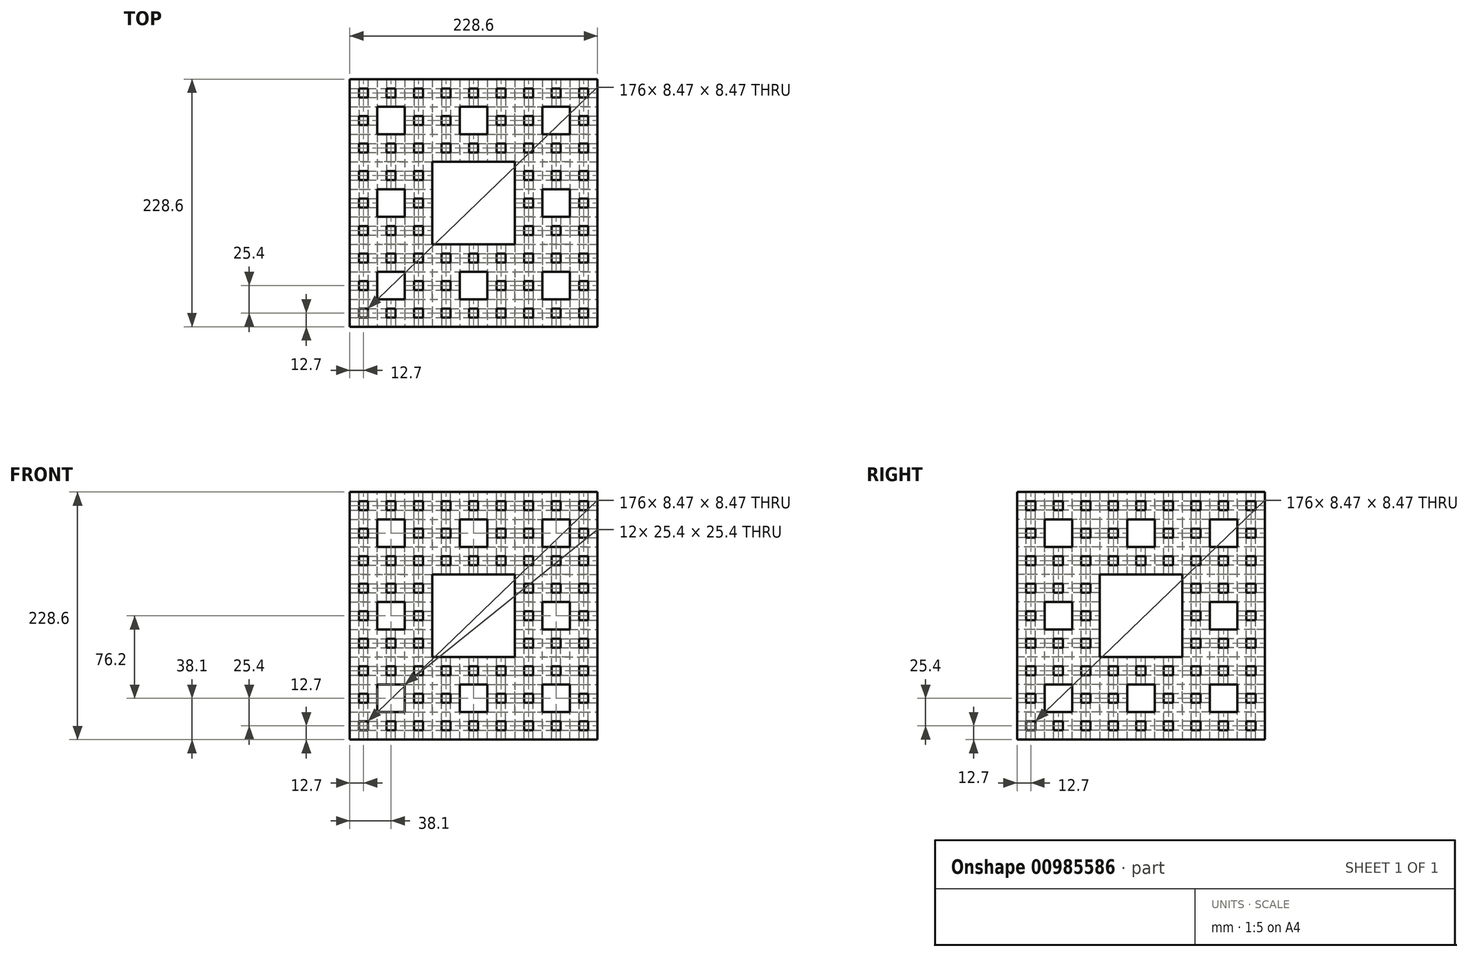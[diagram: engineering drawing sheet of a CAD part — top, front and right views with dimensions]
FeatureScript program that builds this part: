
annotation { "Feature Type Name" : "Feature", "Feature Type Description" : "" }
export const myFeature = defineFeature(function(context is Context, id is Id, definition is map)
    precondition{}
    {
        {
            var Q0;
            Q0=qCreatedBy(makeId("Front.planeOp"),FACE);
            var sketch = newSketch(context, id + "F0", { "sketchPlane" : qUnion([Q0])});
            skLineSegment(sketch, "E0.bottom", {"start": v(114.3, 114.3) * mm, "end": v(-114.3, 114.3) * mm});
            skLineSegment(sketch, "E0.top", {"start": v(114.3, -114.3) * mm, "end": v(-114.3, -114.3) * mm});
            skLineSegment(sketch, "E0.left", {"start": v(114.3, 114.3) * mm, "end": v(114.3, -114.3) * mm});
            skLineSegment(sketch, "E0.right", {"start": v(-114.3, 114.3) * mm, "end": v(-114.3, -114.3) * mm});
            skPoint(sketch, "E0.middle", {"position": v(0, 0) * mm});
            skSolve(sketch);
        }
        {
            var Q0;
            Q0 = qSketchRegion(id + "F0", true);
            extrude(context, id + "F1", {"entities" : qUnion([Q0]), "endBound" : BoundingType.SYMMETRIC, "depth" : 228.6 * mm, "offsetDistance" : 25.4 * mm});
        }
        {
            var Q0;
            Q0=qCreatedBy(makeId("Front.planeOp"),FACE);
            var Q1;
            Q1=qCreatedBy(makeId("Front.planeOp"),FACE);
            var sketch = newSketch(context, id + "F2", { "sketchPlane" : qUnion([Q0, Q1])});
            skLineSegment(sketch, "E1.bottom", {"start": v(38.1, 38.1) * mm, "end": v(-38.1, 38.1) * mm});
            skLineSegment(sketch, "E1.top", {"start": v(38.1, -38.1) * mm, "end": v(-38.1, -38.1) * mm});
            skLineSegment(sketch, "E1.left", {"start": v(38.1, 38.1) * mm, "end": v(38.1, -38.1) * mm});
            skLineSegment(sketch, "E1.right", {"start": v(-38.1, 38.1) * mm, "end": v(-38.1, -38.1) * mm});
            skPoint(sketch, "E1.middle", {"position": v(0, 0) * mm});
            skSolve(sketch);
        }
        {
            var Q0;
            Q0 = qSketchRegion(id + "F2", true);
            extrude(context, id + "F3", {"entities" : qUnion([Q0]), "operationType" : NewBodyOperationType.REMOVE, "endBound" : BoundingType.SYMMETRIC, "oppositeDirection" : true, "depth" : 228.6 * mm, "offsetDistance" : 25.4 * mm});
        }
        {
            var Q0;
            Q0=qCreatedBy(makeId("Right.planeOp"),FACE);
            var Q1;
            Q1=qCreatedBy(makeId("Right.planeOp"),FACE);
            var sketch = newSketch(context, id + "F4", { "sketchPlane" : qUnion([Q0, Q1])});
            skLineSegment(sketch, "E2.bottom", {"start": v(38.1, 38.1) * mm, "end": v(-38.1, 38.1) * mm});
            skLineSegment(sketch, "E2.top", {"start": v(38.1, -38.1) * mm, "end": v(-38.1, -38.1) * mm});
            skLineSegment(sketch, "E2.left", {"start": v(38.1, 38.1) * mm, "end": v(38.1, -38.1) * mm});
            skLineSegment(sketch, "E2.right", {"start": v(-38.1, 38.1) * mm, "end": v(-38.1, -38.1) * mm});
            skPoint(sketch, "E2.middle", {"position": v(0, 0) * mm});
            skSolve(sketch);
        }
        {
            var Q0;
            Q0 = qSketchRegion(id + "F4", true);
            extrude(context, id + "F5", {"entities" : qUnion([Q0]), "operationType" : NewBodyOperationType.REMOVE, "endBound" : BoundingType.SYMMETRIC, "oppositeDirection" : true, "depth" : 228.6 * mm, "offsetDistance" : 25.4 * mm});
        }
        {
            var Q0;
            Q0=qCreatedBy(makeId("Top.planeOp"),FACE);
            var Q1;
            Q1=qCreatedBy(makeId("Top.planeOp"),FACE);
            var sketch = newSketch(context, id + "F6", { "sketchPlane" : qUnion([Q0, Q1])});
            skLineSegment(sketch, "E3.bottom", {"start": v(-38.1, -38.1) * mm, "end": v(38.1, -38.1) * mm});
            skLineSegment(sketch, "E3.top", {"start": v(-38.1, 38.1) * mm, "end": v(38.1, 38.1) * mm});
            skLineSegment(sketch, "E3.left", {"start": v(-38.1, -38.1) * mm, "end": v(-38.1, 38.1) * mm});
            skLineSegment(sketch, "E3.right", {"start": v(38.1, -38.1) * mm, "end": v(38.1, 38.1) * mm});
            skPoint(sketch, "E3.middle", {"position": v(0, 0) * mm});
            skSolve(sketch);
        }
        {
            var Q0;
            Q0 = qSketchRegion(id + "F6", true);
            extrude(context, id + "F7", {"entities" : qUnion([Q0]), "operationType" : NewBodyOperationType.REMOVE, "endBound" : BoundingType.SYMMETRIC, "depth" : 228.6 * mm, "offsetDistance" : 25.4 * mm});
        }
        {
            var Q0;
            Q0=makeQuery(id+"F1.opExtrude","SWEPT_FACE",FACE,{"disambiguationData":[OSD([sQuery(id+"F0.wireOp",EDGE,"E0.left")])]});
            var sketch = newSketch(context, id + "F8", { "sketchPlane" : qUnion([Q0])});
            skSolve(sketch);
        }
        {
            var Q0;
            Q0=makeQuery(id+"F1.opExtrude","CAP_FACE",FACE,{"disambiguationData":[OSD([sQuery(id+"F0.wireOp",EDGE,"E0.bottom"),sQuery(id+"F0.wireOp",EDGE,"E0.top"),sQuery(id+"F0.wireOp",EDGE,"E0.left"),sQuery(id+"F0.wireOp",EDGE,"E0.right")])],"isStart":false});
            var sketch = newSketch(context, id + "F9", { "sketchPlane" : qUnion([Q0])});
            skPoint(sketch, "E4", {"position": v(76.2, 76.2) * mm});
            skPoint(sketch, "E5", {"position": v(0, 76.2) * mm});
            skPoint(sketch, "E6", {"position": v(-76.2, 76.2) * mm});
            skPoint(sketch, "E7", {"position": v(-76.2, 0) * mm});
            skPoint(sketch, "E8", {"position": v(76.2, 0) * mm});
            skPoint(sketch, "E9", {"position": v(76.2, -76.2) * mm});
            skPoint(sketch, "E10", {"position": v(0, -76.2) * mm});
            skPoint(sketch, "E11", {"position": v(-76.2, -76.2) * mm});
            skLineSegment(sketch, "E12.bottom", {"start": v(-63.5, 63.5) * mm, "end": v(-88.9, 63.5) * mm});
            skLineSegment(sketch, "E12.top", {"start": v(-63.5, 88.9) * mm, "end": v(-88.9, 88.9) * mm});
            skLineSegment(sketch, "E12.left", {"start": v(-63.5, 63.5) * mm, "end": v(-63.5, 88.9) * mm});
            skLineSegment(sketch, "E12.right", {"start": v(-88.9, 63.5) * mm, "end": v(-88.9, 88.9) * mm});
            skLineSegment(sketch, "E13.bottom", {"start": v(88.9, 63.5) * mm, "end": v(63.5, 63.5) * mm});
            skLineSegment(sketch, "E13.top", {"start": v(88.9, 88.9) * mm, "end": v(63.5, 88.9) * mm});
            skLineSegment(sketch, "E13.left", {"start": v(88.9, 63.5) * mm, "end": v(88.9, 88.9) * mm});
            skLineSegment(sketch, "E13.right", {"start": v(63.5, 63.5) * mm, "end": v(63.5, 88.9) * mm});
            skLineSegment(sketch, "E14.bottom", {"start": v(12.7, 63.5) * mm, "end": v(-12.7, 63.5) * mm});
            skLineSegment(sketch, "E14.top", {"start": v(12.7, 88.9) * mm, "end": v(-12.7, 88.9) * mm});
            skLineSegment(sketch, "E14.left", {"start": v(12.7, 63.5) * mm, "end": v(12.7, 88.9) * mm});
            skLineSegment(sketch, "E14.right", {"start": v(-12.7, 63.5) * mm, "end": v(-12.7, 88.9) * mm});
            skLineSegment(sketch, "E15.bottom", {"start": v(88.9, -12.7) * mm, "end": v(63.5, -12.7) * mm});
            skLineSegment(sketch, "E15.top", {"start": v(88.9, 12.7) * mm, "end": v(63.5, 12.7) * mm});
            skLineSegment(sketch, "E15.left", {"start": v(88.9, -12.7) * mm, "end": v(88.9, 12.7) * mm});
            skLineSegment(sketch, "E15.right", {"start": v(63.5, -12.7) * mm, "end": v(63.5, 12.7) * mm});
            skLineSegment(sketch, "E16.bottom", {"start": v(63.5, -63.5) * mm, "end": v(88.9, -63.5) * mm});
            skLineSegment(sketch, "E16.top", {"start": v(63.5, -88.9) * mm, "end": v(88.9, -88.9) * mm});
            skLineSegment(sketch, "E16.left", {"start": v(63.5, -63.5) * mm, "end": v(63.5, -88.9) * mm});
            skLineSegment(sketch, "E16.right", {"start": v(88.9, -63.5) * mm, "end": v(88.9, -88.9) * mm});
            skLineSegment(sketch, "E17.bottom", {"start": v(12.7, -63.5) * mm, "end": v(-12.7, -63.5) * mm});
            skLineSegment(sketch, "E17.top", {"start": v(12.7, -88.9) * mm, "end": v(-12.7, -88.9) * mm});
            skLineSegment(sketch, "E17.left", {"start": v(12.7, -63.5) * mm, "end": v(12.7, -88.9) * mm});
            skLineSegment(sketch, "E17.right", {"start": v(-12.7, -63.5) * mm, "end": v(-12.7, -88.9) * mm});
            skLineSegment(sketch, "E18.bottom", {"start": v(-63.5, -63.5) * mm, "end": v(-88.9, -63.5) * mm});
            skLineSegment(sketch, "E18.top", {"start": v(-63.5, -88.9) * mm, "end": v(-88.9, -88.9) * mm});
            skLineSegment(sketch, "E18.left", {"start": v(-63.5, -63.5) * mm, "end": v(-63.5, -88.9) * mm});
            skLineSegment(sketch, "E18.right", {"start": v(-88.9, -63.5) * mm, "end": v(-88.9, -88.9) * mm});
            skLineSegment(sketch, "E19.bottom", {"start": v(-63.5, 12.7) * mm, "end": v(-88.9, 12.7) * mm});
            skLineSegment(sketch, "E19.top", {"start": v(-63.5, -12.7) * mm, "end": v(-88.9, -12.7) * mm});
            skLineSegment(sketch, "E19.left", {"start": v(-63.5, 12.7) * mm, "end": v(-63.5, -12.7) * mm});
            skLineSegment(sketch, "E19.right", {"start": v(-88.9, 12.7) * mm, "end": v(-88.9, -12.7) * mm});
            skSolve(sketch);
        }
        {
            var Q0;
            Q0 = qSketchRegion(id + "F9", true);
            extrude(context, id + "F10", {"entities" : qUnion([Q0]), "operationType" : NewBodyOperationType.REMOVE, "oppositeDirection" : true, "depth" : 228.6 * mm, "offsetDistance" : 25.4 * mm});
        }
        {
            var Q0;
            Q0=makeQuery(id+"F1.opExtrude","CAP_FACE",FACE,{"disambiguationData":[OSD([sQuery(id+"F0.wireOp",EDGE,"E0.bottom"),sQuery(id+"F0.wireOp",EDGE,"E0.top"),sQuery(id+"F0.wireOp",EDGE,"E0.left"),sQuery(id+"F0.wireOp",EDGE,"E0.right")])],"isStart":false});
            var sketch = newSketch(context, id + "F11", { "sketchPlane" : qUnion([Q0])});
            skPoint(sketch, "E20", {"position": v(-101.6, 101.6) * mm});
            skPoint(sketch, "E21", {"position": v(-76.2, 101.6) * mm});
            skPoint(sketch, "E22", {"position": v(-50.8, 101.6) * mm});
            skPoint(sketch, "E23", {"position": v(-50.8, 76.2) * mm});
            skPoint(sketch, "E24", {"position": v(-50.8, 50.8) * mm});
            skPoint(sketch, "E25", {"position": v(-76.2, 50.8) * mm});
            skPoint(sketch, "E26", {"position": v(-101.6, 50.8) * mm});
            skPoint(sketch, "E27", {"position": v(-101.6, 76.2) * mm});
            skPoint(sketch, "E28", {"position": v(-76.2, 88.9) * mm});
            skPoint(sketch, "E29", {"position": v(-76.2, 63.5) * mm});
            skPoint(sketch, "E30", {"position": v(-88.9, 76.2) * mm});
            skPoint(sketch, "E31", {"position": v(-63.5, 76.2) * mm});
            skLineSegment(sketch, "E32.bottom", {"start": v(-97.37, 105.83) * mm, "end": v(-105.83, 105.83) * mm});
            skLineSegment(sketch, "E32.top", {"start": v(-97.37, 97.37) * mm, "end": v(-105.83, 97.37) * mm});
            skLineSegment(sketch, "E32.left", {"start": v(-97.37, 105.83) * mm, "end": v(-97.37, 97.37) * mm});
            skLineSegment(sketch, "E32.right", {"start": v(-105.83, 105.83) * mm, "end": v(-105.83, 97.37) * mm});
            skLineSegment(sketch, "E33.bottom", {"start": v(-71.97, 105.83) * mm, "end": v(-80.43, 105.83) * mm});
            skLineSegment(sketch, "E33.top", {"start": v(-71.97, 97.37) * mm, "end": v(-80.43, 97.37) * mm});
            skLineSegment(sketch, "E33.left", {"start": v(-71.97, 105.83) * mm, "end": v(-71.97, 97.37) * mm});
            skLineSegment(sketch, "E33.right", {"start": v(-80.43, 105.83) * mm, "end": v(-80.43, 97.37) * mm});
            skLineSegment(sketch, "E34.bottom", {"start": v(-46.57, 105.83) * mm, "end": v(-55.03, 105.83) * mm});
            skLineSegment(sketch, "E34.top", {"start": v(-46.57, 97.37) * mm, "end": v(-55.03, 97.37) * mm});
            skLineSegment(sketch, "E34.left", {"start": v(-46.57, 105.83) * mm, "end": v(-46.57, 97.37) * mm});
            skLineSegment(sketch, "E34.right", {"start": v(-55.03, 105.83) * mm, "end": v(-55.03, 97.37) * mm});
            skLineSegment(sketch, "E35.bottom", {"start": v(-46.57, 80.43) * mm, "end": v(-55.03, 80.43) * mm});
            skLineSegment(sketch, "E35.top", {"start": v(-46.57, 71.97) * mm, "end": v(-55.03, 71.97) * mm});
            skLineSegment(sketch, "E35.left", {"start": v(-46.57, 80.43) * mm, "end": v(-46.57, 71.97) * mm});
            skLineSegment(sketch, "E35.right", {"start": v(-55.03, 80.43) * mm, "end": v(-55.03, 71.97) * mm});
            skLineSegment(sketch, "E36.bottom", {"start": v(-55.03, 55.03) * mm, "end": v(-46.57, 55.03) * mm});
            skLineSegment(sketch, "E36.top", {"start": v(-55.03, 46.57) * mm, "end": v(-46.57, 46.57) * mm});
            skLineSegment(sketch, "E36.left", {"start": v(-55.03, 55.03) * mm, "end": v(-55.03, 46.57) * mm});
            skLineSegment(sketch, "E36.right", {"start": v(-46.57, 55.03) * mm, "end": v(-46.57, 46.57) * mm});
            skLineSegment(sketch, "E37.bottom", {"start": v(-71.97, 55.03) * mm, "end": v(-80.43, 55.03) * mm});
            skLineSegment(sketch, "E37.top", {"start": v(-71.97, 46.57) * mm, "end": v(-80.43, 46.57) * mm});
            skLineSegment(sketch, "E37.left", {"start": v(-71.97, 55.03) * mm, "end": v(-71.97, 46.57) * mm});
            skLineSegment(sketch, "E37.right", {"start": v(-80.43, 55.03) * mm, "end": v(-80.43, 46.57) * mm});
            skLineSegment(sketch, "E38.bottom", {"start": v(-97.37, 55.03) * mm, "end": v(-105.83, 55.03) * mm});
            skLineSegment(sketch, "E38.top", {"start": v(-97.37, 46.57) * mm, "end": v(-105.83, 46.57) * mm});
            skLineSegment(sketch, "E38.left", {"start": v(-97.37, 55.03) * mm, "end": v(-97.37, 46.57) * mm});
            skLineSegment(sketch, "E38.right", {"start": v(-105.83, 55.03) * mm, "end": v(-105.83, 46.57) * mm});
            skLineSegment(sketch, "E39.bottom", {"start": v(-97.37, 80.43) * mm, "end": v(-105.83, 80.43) * mm});
            skLineSegment(sketch, "E39.top", {"start": v(-97.37, 71.97) * mm, "end": v(-105.83, 71.97) * mm});
            skLineSegment(sketch, "E39.left", {"start": v(-97.37, 80.43) * mm, "end": v(-97.37, 71.97) * mm});
            skLineSegment(sketch, "E39.right", {"start": v(-105.83, 80.43) * mm, "end": v(-105.83, 71.97) * mm});
            skLineSegment(sketch, "E40.MirrorCS", {"start": v(71.97, 55.03) * mm, "end": v(80.43, 55.03) * mm});
            skLineSegment(sketch, "E41.MirrorCS", {"start": v(55.03, 80.43) * mm, "end": v(55.03, 71.97) * mm});
            skLineSegment(sketch, "E42.MirrorCS", {"start": v(46.57, 80.43) * mm, "end": v(46.57, 71.97) * mm});
            skLineSegment(sketch, "E43.MirrorCS", {"start": v(97.37, 80.43) * mm, "end": v(97.37, 71.97) * mm});
            skLineSegment(sketch, "E44.MirrorCS", {"start": v(71.97, 55.03) * mm, "end": v(71.97, 46.57) * mm});
            skLineSegment(sketch, "E45.MirrorCS", {"start": v(80.43, 105.83) * mm, "end": v(80.43, 97.37) * mm});
            skLineSegment(sketch, "E46.MirrorCS", {"start": v(46.57, 97.37) * mm, "end": v(55.03, 97.37) * mm});
            skLineSegment(sketch, "E47.MirrorCS", {"start": v(97.37, 105.83) * mm, "end": v(97.37, 97.37) * mm});
            skLineSegment(sketch, "E48.MirrorCS", {"start": v(71.97, 105.83) * mm, "end": v(71.97, 97.37) * mm});
            skLineSegment(sketch, "E49.MirrorCS", {"start": v(97.37, 71.97) * mm, "end": v(105.83, 71.97) * mm});
            skLineSegment(sketch, "E50.MirrorCS", {"start": v(71.97, 46.57) * mm, "end": v(80.43, 46.57) * mm});
            skLineSegment(sketch, "E51.MirrorCS", {"start": v(97.37, 80.43) * mm, "end": v(105.83, 80.43) * mm});
            skLineSegment(sketch, "E52.MirrorCS", {"start": v(55.03, 105.83) * mm, "end": v(55.03, 97.37) * mm});
            skLineSegment(sketch, "E53.MirrorCS", {"start": v(46.57, 105.83) * mm, "end": v(55.03, 105.83) * mm});
            skLineSegment(sketch, "E54.MirrorCS", {"start": v(80.43, 55.03) * mm, "end": v(80.43, 46.57) * mm});
            skLineSegment(sketch, "E55.MirrorCS", {"start": v(105.83, 55.03) * mm, "end": v(105.83, 46.57) * mm});
            skLineSegment(sketch, "E56.MirrorCS", {"start": v(97.37, 97.37) * mm, "end": v(105.83, 97.37) * mm});
            skLineSegment(sketch, "E57.MirrorCS", {"start": v(97.37, 105.83) * mm, "end": v(105.83, 105.83) * mm});
            skLineSegment(sketch, "E58.MirrorCS", {"start": v(97.37, 55.03) * mm, "end": v(97.37, 46.57) * mm});
            skLineSegment(sketch, "E59.MirrorCS", {"start": v(46.57, 80.43) * mm, "end": v(55.03, 80.43) * mm});
            skLineSegment(sketch, "E60.MirrorCS", {"start": v(105.83, 105.83) * mm, "end": v(105.83, 97.37) * mm});
            skLineSegment(sketch, "E61.MirrorCS", {"start": v(55.03, 46.57) * mm, "end": v(46.57, 46.57) * mm});
            skLineSegment(sketch, "E62.MirrorCS", {"start": v(55.03, 55.03) * mm, "end": v(55.03, 46.57) * mm});
            skLineSegment(sketch, "E63.MirrorCS", {"start": v(71.97, 105.83) * mm, "end": v(80.43, 105.83) * mm});
            skLineSegment(sketch, "E64.MirrorCS", {"start": v(71.97, 97.37) * mm, "end": v(80.43, 97.37) * mm});
            skLineSegment(sketch, "E65.MirrorCS", {"start": v(97.37, 55.03) * mm, "end": v(105.83, 55.03) * mm});
            skLineSegment(sketch, "E66.MirrorCS", {"start": v(105.83, 80.43) * mm, "end": v(105.83, 71.97) * mm});
            skLineSegment(sketch, "E67.MirrorCS", {"start": v(97.37, 46.57) * mm, "end": v(105.83, 46.57) * mm});
            skLineSegment(sketch, "E68.MirrorCS", {"start": v(55.03, 55.03) * mm, "end": v(46.57, 55.03) * mm});
            skLineSegment(sketch, "E69.MirrorCS", {"start": v(46.57, 71.97) * mm, "end": v(55.03, 71.97) * mm});
            skLineSegment(sketch, "E70.MirrorCS", {"start": v(46.57, 105.83) * mm, "end": v(46.57, 97.37) * mm});
            skLineSegment(sketch, "E71.MirrorCS", {"start": v(46.57, 55.03) * mm, "end": v(46.57, 46.57) * mm});
            skPoint(sketch, "E72.MirrorP", {"position": v(50.8, 101.6) * mm});
            skPoint(sketch, "E73.MirrorP", {"position": v(101.6, 76.2) * mm});
            skPoint(sketch, "E74.MirrorP", {"position": v(88.9, 76.2) * mm});
            skPoint(sketch, "E75.MirrorP", {"position": v(50.45, 76.2) * mm});
            skPoint(sketch, "E76.MirrorP", {"position": v(76.2, 101.6) * mm});
            skPoint(sketch, "E77.MirrorP", {"position": v(101.6, 50.8) * mm});
            skPoint(sketch, "E78.MirrorP", {"position": v(76.2, 50.8) * mm});
            skPoint(sketch, "E79.MirrorP", {"position": v(101.6, 101.6) * mm});
            skPoint(sketch, "E80.MirrorP", {"position": v(50.8, 50.8) * mm});
            skPoint(sketch, "E81.MirrorP", {"position": v(63.5, 76.2) * mm});
            skPoint(sketch, "E82.MirrorP", {"position": v(76.2, 88.9) * mm});
            skPoint(sketch, "E83.MirrorP", {"position": v(76.2, 63.5) * mm});
            skLineSegment(sketch, "E84.MirrorCS", {"start": v(-46.57, -80.43) * mm, "end": v(-55.03, -80.43) * mm});
            skLineSegment(sketch, "E85.MirrorCS", {"start": v(-46.57, -97.37) * mm, "end": v(-55.03, -97.37) * mm});
            skLineSegment(sketch, "E86.MirrorCS", {"start": v(-55.03, -105.83) * mm, "end": v(-55.03, -97.37) * mm});
            skLineSegment(sketch, "E87.MirrorCS", {"start": v(-46.57, -105.83) * mm, "end": v(-46.57, -97.37) * mm});
            skLineSegment(sketch, "E88.MirrorCS", {"start": v(-46.57, -105.83) * mm, "end": v(-55.03, -105.83) * mm});
            skLineSegment(sketch, "E89.MirrorCS", {"start": v(-71.97, -55.03) * mm, "end": v(-80.43, -55.03) * mm});
            skLineSegment(sketch, "E90.MirrorCS", {"start": v(-55.03, -80.43) * mm, "end": v(-55.03, -71.97) * mm});
            skLineSegment(sketch, "E91.MirrorCS", {"start": v(-105.83, -80.43) * mm, "end": v(-105.83, -71.97) * mm});
            skLineSegment(sketch, "E92.MirrorCS", {"start": v(-71.97, -46.57) * mm, "end": v(-80.43, -46.57) * mm});
            skLineSegment(sketch, "E93.MirrorCS", {"start": v(105.83, -105.83) * mm, "end": v(105.83, -97.37) * mm});
            skLineSegment(sketch, "E94.MirrorCS", {"start": v(97.37, -55.03) * mm, "end": v(97.37, -46.57) * mm});
            skPoint(sketch, "E95.MirrorP", {"position": v(-50.8, -101.6) * mm});
            skLineSegment(sketch, "E96.MirrorCS", {"start": v(46.57, -105.83) * mm, "end": v(46.57, -97.37) * mm});
            skLineSegment(sketch, "E97.MirrorCS", {"start": v(71.97, -46.57) * mm, "end": v(80.43, -46.57) * mm});
            skLineSegment(sketch, "E98.MirrorCS", {"start": v(-97.37, -105.83) * mm, "end": v(-97.37, -97.37) * mm});
            skLineSegment(sketch, "E99.MirrorCS", {"start": v(80.43, -55.03) * mm, "end": v(80.43, -46.57) * mm});
            skLineSegment(sketch, "E100.MirrorCS", {"start": v(-97.37, -55.03) * mm, "end": v(-97.37, -46.57) * mm});
            skLineSegment(sketch, "E101.MirrorCS", {"start": v(97.37, -105.83) * mm, "end": v(97.37, -97.37) * mm});
            skLineSegment(sketch, "E102.MirrorCS", {"start": v(-71.97, -105.83) * mm, "end": v(-71.97, -97.37) * mm});
            skLineSegment(sketch, "E103.MirrorCS", {"start": v(46.57, -105.83) * mm, "end": v(55.03, -105.83) * mm});
            skLineSegment(sketch, "E104.MirrorCS", {"start": v(-46.57, -71.97) * mm, "end": v(-55.03, -71.97) * mm});
            skLineSegment(sketch, "E105.MirrorCS", {"start": v(55.03, -55.03) * mm, "end": v(46.57, -55.03) * mm});
            skLineSegment(sketch, "E106.MirrorCS", {"start": v(55.03, -46.57) * mm, "end": v(46.57, -46.57) * mm});
            skLineSegment(sketch, "E107.MirrorCS", {"start": v(97.37, -55.03) * mm, "end": v(105.83, -55.03) * mm});
            skLineSegment(sketch, "E108.MirrorCS", {"start": v(-97.37, -80.43) * mm, "end": v(-105.83, -80.43) * mm});
            skLineSegment(sketch, "E109.MirrorCS", {"start": v(46.57, -80.43) * mm, "end": v(55.03, -80.43) * mm});
            skLineSegment(sketch, "E110.MirrorCS", {"start": v(97.37, -80.43) * mm, "end": v(105.83, -80.43) * mm});
            skLineSegment(sketch, "E111.MirrorCS", {"start": v(97.37, -105.83) * mm, "end": v(105.83, -105.83) * mm});
            skLineSegment(sketch, "E112.MirrorCS", {"start": v(80.43, -105.83) * mm, "end": v(80.43, -97.37) * mm});
            skLineSegment(sketch, "E113.MirrorCS", {"start": v(-71.97, -55.03) * mm, "end": v(-71.97, -46.57) * mm});
            skLineSegment(sketch, "E114.MirrorCS", {"start": v(-97.37, -55.03) * mm, "end": v(-105.83, -55.03) * mm});
            skLineSegment(sketch, "E115.MirrorCS", {"start": v(55.03, -105.83) * mm, "end": v(55.03, -97.37) * mm});
            skLineSegment(sketch, "E116.MirrorCS", {"start": v(-97.37, -71.97) * mm, "end": v(-105.83, -71.97) * mm});
            skLineSegment(sketch, "E117.MirrorCS", {"start": v(97.37, -80.43) * mm, "end": v(97.37, -71.97) * mm});
            skLineSegment(sketch, "E118.MirrorCS", {"start": v(105.83, -55.03) * mm, "end": v(105.83, -46.57) * mm});
            skLineSegment(sketch, "E119.MirrorCS", {"start": v(97.37, -46.57) * mm, "end": v(105.83, -46.57) * mm});
            skLineSegment(sketch, "E120.MirrorCS", {"start": v(-46.57, -80.43) * mm, "end": v(-46.57, -71.97) * mm});
            skLineSegment(sketch, "E121.MirrorCS", {"start": v(-55.03, -55.03) * mm, "end": v(-55.03, -46.57) * mm});
            skLineSegment(sketch, "E122.MirrorCS", {"start": v(-105.83, -55.03) * mm, "end": v(-105.83, -46.57) * mm});
            skLineSegment(sketch, "E123.MirrorCS", {"start": v(-97.37, -46.57) * mm, "end": v(-105.83, -46.57) * mm});
            skLineSegment(sketch, "E124.MirrorCS", {"start": v(46.57, -55.03) * mm, "end": v(46.57, -46.57) * mm});
            skLineSegment(sketch, "E125.MirrorCS", {"start": v(71.97, -105.83) * mm, "end": v(80.43, -105.83) * mm});
            skLineSegment(sketch, "E126.MirrorCS", {"start": v(-80.43, -105.83) * mm, "end": v(-80.43, -97.37) * mm});
            skLineSegment(sketch, "E127.MirrorCS", {"start": v(46.57, -80.43) * mm, "end": v(46.57, -71.97) * mm});
            skLineSegment(sketch, "E128.MirrorCS", {"start": v(-80.43, -55.03) * mm, "end": v(-80.43, -46.57) * mm});
            skLineSegment(sketch, "E129.MirrorCS", {"start": v(105.83, -80.43) * mm, "end": v(105.83, -71.97) * mm});
            skLineSegment(sketch, "E130.MirrorCS", {"start": v(71.97, -55.03) * mm, "end": v(71.97, -46.57) * mm});
            skLineSegment(sketch, "E131.MirrorCS", {"start": v(71.97, -105.83) * mm, "end": v(71.97, -97.37) * mm});
            skLineSegment(sketch, "E132.MirrorCS", {"start": v(46.57, -97.37) * mm, "end": v(55.03, -97.37) * mm});
            skLineSegment(sketch, "E133.MirrorCS", {"start": v(-55.03, -46.57) * mm, "end": v(-46.57, -46.57) * mm});
            skLineSegment(sketch, "E134.MirrorCS", {"start": v(-97.37, -105.83) * mm, "end": v(-105.83, -105.83) * mm});
            skLineSegment(sketch, "E135.MirrorCS", {"start": v(-55.03, -55.03) * mm, "end": v(-46.57, -55.03) * mm});
            skLineSegment(sketch, "E136.MirrorCS", {"start": v(-105.83, -105.83) * mm, "end": v(-105.83, -97.37) * mm});
            skLineSegment(sketch, "E137.MirrorCS", {"start": v(97.37, -97.37) * mm, "end": v(105.83, -97.37) * mm});
            skLineSegment(sketch, "E138.MirrorCS", {"start": v(46.57, -71.97) * mm, "end": v(55.03, -71.97) * mm});
            skLineSegment(sketch, "E139.MirrorCS", {"start": v(55.03, -80.43) * mm, "end": v(55.03, -71.97) * mm});
            skLineSegment(sketch, "E140.MirrorCS", {"start": v(-71.97, -97.37) * mm, "end": v(-80.43, -97.37) * mm});
            skLineSegment(sketch, "E141.MirrorCS", {"start": v(-46.57, -55.03) * mm, "end": v(-46.57, -46.57) * mm});
            skLineSegment(sketch, "E142.MirrorCS", {"start": v(71.97, -55.03) * mm, "end": v(80.43, -55.03) * mm});
            skLineSegment(sketch, "E143.MirrorCS", {"start": v(-97.37, -80.43) * mm, "end": v(-97.37, -71.97) * mm});
            skLineSegment(sketch, "E144.MirrorCS", {"start": v(55.03, -55.03) * mm, "end": v(55.03, -46.57) * mm});
            skLineSegment(sketch, "E145.MirrorCS", {"start": v(97.37, -71.97) * mm, "end": v(105.83, -71.97) * mm});
            skLineSegment(sketch, "E146.MirrorCS", {"start": v(-97.37, -97.37) * mm, "end": v(-105.83, -97.37) * mm});
            skLineSegment(sketch, "E147.MirrorCS", {"start": v(71.97, -97.37) * mm, "end": v(80.43, -97.37) * mm});
            skLineSegment(sketch, "E148.MirrorCS", {"start": v(-71.97, -105.83) * mm, "end": v(-80.43, -105.83) * mm});
            skPoint(sketch, "E149.MirrorP", {"position": v(-50.8, -76.2) * mm});
            skPoint(sketch, "E150.MirrorP", {"position": v(-76.2, -101.6) * mm});
            skPoint(sketch, "E151.MirrorP", {"position": v(-101.6, -50.8) * mm});
            skPoint(sketch, "E152.MirrorP", {"position": v(50.8, -50.8) * mm});
            skPoint(sketch, "E153.MirrorP", {"position": v(-101.6, -76.2) * mm});
            skPoint(sketch, "E154.MirrorP", {"position": v(76.2, -101.6) * mm});
            skPoint(sketch, "E155.MirrorP", {"position": v(101.6, -101.6) * mm});
            skPoint(sketch, "E156.MirrorP", {"position": v(50.8, -76.2) * mm});
            skPoint(sketch, "E157.MirrorP", {"position": v(-76.2, -50.8) * mm});
            skPoint(sketch, "E158.MirrorP", {"position": v(76.2, -50.8) * mm});
            skPoint(sketch, "E159.MirrorP", {"position": v(-50.8, -50.8) * mm});
            skPoint(sketch, "E160.MirrorP", {"position": v(-101.6, -101.6) * mm});
            skPoint(sketch, "E161.MirrorP", {"position": v(101.6, -50.8) * mm});
            skPoint(sketch, "E162.MirrorP", {"position": v(101.6, -76.2) * mm});
            skPoint(sketch, "E163.MirrorP", {"position": v(50.8, -101.6) * mm});
            skPoint(sketch, "E164.MirrorP", {"position": v(-63.5, -76.2) * mm});
            skPoint(sketch, "E165.MirrorP", {"position": v(-76.2, -88.9) * mm});
            skPoint(sketch, "E166.MirrorP", {"position": v(-76.2, -63.5) * mm});
            skPoint(sketch, "E167.MirrorP", {"position": v(63.5, -76.2) * mm});
            skPoint(sketch, "E168.MirrorP", {"position": v(76.2, -63.5) * mm});
            skPoint(sketch, "E169.MirrorP", {"position": v(-88.9, -76.2) * mm});
            skPoint(sketch, "E170.MirrorP", {"position": v(88.9, -76.2) * mm});
            skPoint(sketch, "E171.MirrorP", {"position": v(76.2, -88.9) * mm});
            skPoint(sketch, "E172", {"position": v(-50.8, 0) * mm});
            skPoint(sketch, "E172.positionSnap0", {"position": v(-50.8, 46.57) * mm});
            skPoint(sketch, "E173", {"position": v(-76.2, 25.4) * mm});
            skPoint(sketch, "E174", {"position": v(-76.2, -25.4) * mm});
            skPoint(sketch, "E175", {"position": v(-101.6, -25.4) * mm});
            skPoint(sketch, "E176", {"position": v(-101.6, 0) * mm});
            skPoint(sketch, "E177", {"position": v(-50.8, 25.4) * mm});
            skPoint(sketch, "E178", {"position": v(-50.8, -25.4) * mm});
            skPoint(sketch, "E179", {"position": v(-101.6, 25.4) * mm});
            skLineSegment(sketch, "E180.bottom", {"start": v(-97.37, 29.63) * mm, "end": v(-105.83, 29.63) * mm});
            skLineSegment(sketch, "E180.top", {"start": v(-97.37, 21.17) * mm, "end": v(-105.83, 21.17) * mm});
            skLineSegment(sketch, "E180.left", {"start": v(-97.37, 29.63) * mm, "end": v(-97.37, 21.17) * mm});
            skLineSegment(sketch, "E180.right", {"start": v(-105.83, 29.63) * mm, "end": v(-105.83, 21.17) * mm});
            skLineSegment(sketch, "E181.bottom", {"start": v(-71.97, 29.63) * mm, "end": v(-80.43, 29.63) * mm});
            skLineSegment(sketch, "E181.top", {"start": v(-71.97, 21.17) * mm, "end": v(-80.43, 21.17) * mm});
            skLineSegment(sketch, "E181.left", {"start": v(-71.97, 29.63) * mm, "end": v(-71.97, 21.17) * mm});
            skLineSegment(sketch, "E181.right", {"start": v(-80.43, 29.63) * mm, "end": v(-80.43, 21.17) * mm});
            skLineSegment(sketch, "E182.bottom", {"start": v(-46.57, 29.63) * mm, "end": v(-55.03, 29.63) * mm});
            skLineSegment(sketch, "E182.top", {"start": v(-46.57, 21.17) * mm, "end": v(-55.03, 21.17) * mm});
            skLineSegment(sketch, "E182.left", {"start": v(-46.57, 29.63) * mm, "end": v(-46.57, 21.17) * mm});
            skLineSegment(sketch, "E182.right", {"start": v(-55.03, 29.63) * mm, "end": v(-55.03, 21.17) * mm});
            skLineSegment(sketch, "E183.bottom", {"start": v(-46.57, 4.23) * mm, "end": v(-55.03, 4.23) * mm});
            skLineSegment(sketch, "E183.top", {"start": v(-46.57, -4.23) * mm, "end": v(-55.03, -4.23) * mm});
            skLineSegment(sketch, "E183.left", {"start": v(-46.57, 4.23) * mm, "end": v(-46.57, -4.23) * mm});
            skLineSegment(sketch, "E183.right", {"start": v(-55.03, 4.23) * mm, "end": v(-55.03, -4.23) * mm});
            skLineSegment(sketch, "E184.bottom", {"start": v(-46.57, -21.17) * mm, "end": v(-55.03, -21.17) * mm});
            skLineSegment(sketch, "E184.top", {"start": v(-46.57, -29.63) * mm, "end": v(-55.03, -29.63) * mm});
            skLineSegment(sketch, "E184.left", {"start": v(-46.57, -21.17) * mm, "end": v(-46.57, -29.63) * mm});
            skLineSegment(sketch, "E184.right", {"start": v(-55.03, -21.17) * mm, "end": v(-55.03, -29.63) * mm});
            skLineSegment(sketch, "E185.bottom", {"start": v(-71.97, -21.17) * mm, "end": v(-80.43, -21.17) * mm});
            skLineSegment(sketch, "E185.top", {"start": v(-71.97, -29.63) * mm, "end": v(-80.43, -29.63) * mm});
            skLineSegment(sketch, "E185.left", {"start": v(-71.97, -21.17) * mm, "end": v(-71.97, -29.63) * mm});
            skLineSegment(sketch, "E185.right", {"start": v(-80.43, -21.17) * mm, "end": v(-80.43, -29.63) * mm});
            skLineSegment(sketch, "E186.bottom", {"start": v(-97.37, -21.17) * mm, "end": v(-105.83, -21.17) * mm});
            skLineSegment(sketch, "E186.top", {"start": v(-97.37, -29.63) * mm, "end": v(-105.83, -29.63) * mm});
            skLineSegment(sketch, "E186.left", {"start": v(-97.37, -21.17) * mm, "end": v(-97.37, -29.63) * mm});
            skLineSegment(sketch, "E186.right", {"start": v(-105.83, -21.17) * mm, "end": v(-105.83, -29.63) * mm});
            skLineSegment(sketch, "E187.bottom", {"start": v(-97.37, 4.23) * mm, "end": v(-105.83, 4.23) * mm});
            skLineSegment(sketch, "E187.top", {"start": v(-97.37, -4.23) * mm, "end": v(-105.83, -4.23) * mm});
            skLineSegment(sketch, "E187.left", {"start": v(-97.37, 4.23) * mm, "end": v(-97.37, -4.23) * mm});
            skLineSegment(sketch, "E187.right", {"start": v(-105.83, 4.23) * mm, "end": v(-105.83, -4.23) * mm});
            skLineSegment(sketch, "E188.MirrorCS", {"start": v(97.37, -4.23) * mm, "end": v(105.83, -4.23) * mm});
            skLineSegment(sketch, "E189.MirrorCS", {"start": v(55.03, 4.23) * mm, "end": v(55.03, -4.23) * mm});
            skLineSegment(sketch, "E190.MirrorCS", {"start": v(71.97, 29.63) * mm, "end": v(71.97, 21.17) * mm});
            skLineSegment(sketch, "E191.MirrorCS", {"start": v(97.37, 21.17) * mm, "end": v(105.83, 21.17) * mm});
            skLineSegment(sketch, "E192.MirrorCS", {"start": v(105.83, -21.17) * mm, "end": v(105.83, -29.63) * mm});
            skLineSegment(sketch, "E193.MirrorCS", {"start": v(55.03, -21.17) * mm, "end": v(55.03, -29.63) * mm});
            skLineSegment(sketch, "E194.MirrorCS", {"start": v(46.57, -21.17) * mm, "end": v(46.57, -29.63) * mm});
            skLineSegment(sketch, "E195.MirrorCS", {"start": v(46.57, 21.17) * mm, "end": v(55.03, 21.17) * mm});
            skLineSegment(sketch, "E196.MirrorCS", {"start": v(97.37, -21.17) * mm, "end": v(97.37, -29.63) * mm});
            skLineSegment(sketch, "E197.MirrorCS", {"start": v(97.37, -29.63) * mm, "end": v(105.83, -29.63) * mm});
            skLineSegment(sketch, "E198.MirrorCS", {"start": v(80.43, -21.17) * mm, "end": v(80.43, -29.63) * mm});
            skLineSegment(sketch, "E199.MirrorCS", {"start": v(80.43, 29.63) * mm, "end": v(80.43, 21.17) * mm});
            skLineSegment(sketch, "E200.MirrorCS", {"start": v(46.57, -4.23) * mm, "end": v(55.03, -4.23) * mm});
            skLineSegment(sketch, "E201.MirrorCS", {"start": v(71.97, -21.17) * mm, "end": v(71.97, -29.63) * mm});
            skLineSegment(sketch, "E202.MirrorCS", {"start": v(46.57, -21.17) * mm, "end": v(55.03, -21.17) * mm});
            skLineSegment(sketch, "E203.MirrorCS", {"start": v(46.57, 4.23) * mm, "end": v(55.03, 4.23) * mm});
            skLineSegment(sketch, "E204.MirrorCS", {"start": v(46.57, 4.23) * mm, "end": v(46.57, -4.23) * mm});
            skLineSegment(sketch, "E205.MirrorCS", {"start": v(71.97, 21.17) * mm, "end": v(80.43, 21.17) * mm});
            skLineSegment(sketch, "E206.MirrorCS", {"start": v(97.37, 29.63) * mm, "end": v(105.83, 29.63) * mm});
            skLineSegment(sketch, "E207.MirrorCS", {"start": v(55.03, 29.63) * mm, "end": v(55.03, 21.17) * mm});
            skLineSegment(sketch, "E208.MirrorCS", {"start": v(46.57, -29.63) * mm, "end": v(55.03, -29.63) * mm});
            skLineSegment(sketch, "E209.MirrorCS", {"start": v(97.37, -21.17) * mm, "end": v(105.83, -21.17) * mm});
            skLineSegment(sketch, "E210.MirrorCS", {"start": v(71.97, -29.63) * mm, "end": v(80.43, -29.63) * mm});
            skLineSegment(sketch, "E211.MirrorCS", {"start": v(97.37, 4.23) * mm, "end": v(97.37, -4.23) * mm});
            skLineSegment(sketch, "E212.MirrorCS", {"start": v(71.97, 29.63) * mm, "end": v(80.43, 29.63) * mm});
            skLineSegment(sketch, "E213.MirrorCS", {"start": v(97.37, 29.63) * mm, "end": v(97.37, 21.17) * mm});
            skLineSegment(sketch, "E214.MirrorCS", {"start": v(97.37, 4.23) * mm, "end": v(105.83, 4.23) * mm});
            skLineSegment(sketch, "E215.MirrorCS", {"start": v(105.83, 29.63) * mm, "end": v(105.83, 21.17) * mm});
            skLineSegment(sketch, "E216.MirrorCS", {"start": v(46.57, 29.63) * mm, "end": v(55.03, 29.63) * mm});
            skLineSegment(sketch, "E217.MirrorCS", {"start": v(105.83, 4.23) * mm, "end": v(105.83, -4.23) * mm});
            skLineSegment(sketch, "E218.MirrorCS", {"start": v(71.97, -21.17) * mm, "end": v(80.43, -21.17) * mm});
            skLineSegment(sketch, "E219.MirrorCS", {"start": v(46.57, 29.63) * mm, "end": v(46.57, 21.17) * mm});
            skPoint(sketch, "E220.MirrorP", {"position": v(101.6, -25.4) * mm});
            skPoint(sketch, "E221.MirrorP", {"position": v(76.2, -25.4) * mm});
            skPoint(sketch, "E222.MirrorP", {"position": v(50.8, 0) * mm});
            skPoint(sketch, "E223.MirrorP", {"position": v(101.6, 25.4) * mm});
            skPoint(sketch, "E224.MirrorP", {"position": v(50.8, 25.4) * mm});
            skPoint(sketch, "E225.MirrorP", {"position": v(76.2, 25.4) * mm});
            skPoint(sketch, "E226.MirrorP", {"position": v(101.6, 0) * mm});
            skPoint(sketch, "E227.MirrorP", {"position": v(50.8, -25.4) * mm});
            skPoint(sketch, "E228", {"position": v(0, 101.6) * mm});
            skPoint(sketch, "E229", {"position": v(0, 76.2) * mm});
            skPoint(sketch, "E230", {"position": v(25.4, 76.2) * mm});
            skPoint(sketch, "E231", {"position": v(-25.4, 76.2) * mm});
            skPoint(sketch, "E232", {"position": v(0, 50.8) * mm});
            skPoint(sketch, "E233", {"position": v(25.4, 101.6) * mm});
            skPoint(sketch, "E234", {"position": v(25.4, 50.8) * mm});
            skPoint(sketch, "E235", {"position": v(-25.4, 50.8) * mm});
            skPoint(sketch, "E236", {"position": v(-25.4, 101.6) * mm});
            skLineSegment(sketch, "E237.bottom", {"start": v(-21.17, 105.83) * mm, "end": v(-29.63, 105.83) * mm});
            skLineSegment(sketch, "E237.top", {"start": v(-21.17, 97.37) * mm, "end": v(-29.63, 97.37) * mm});
            skLineSegment(sketch, "E237.left", {"start": v(-21.17, 105.83) * mm, "end": v(-21.17, 97.37) * mm});
            skLineSegment(sketch, "E237.right", {"start": v(-29.63, 105.83) * mm, "end": v(-29.63, 97.37) * mm});
            skLineSegment(sketch, "E238.bottom", {"start": v(4.23, 105.83) * mm, "end": v(-4.23, 105.83) * mm});
            skLineSegment(sketch, "E238.top", {"start": v(4.23, 97.37) * mm, "end": v(-4.23, 97.37) * mm});
            skLineSegment(sketch, "E238.left", {"start": v(4.23, 105.83) * mm, "end": v(4.23, 97.37) * mm});
            skLineSegment(sketch, "E238.right", {"start": v(-4.23, 105.83) * mm, "end": v(-4.23, 97.37) * mm});
            skLineSegment(sketch, "E239.bottom", {"start": v(21.17, 105.83) * mm, "end": v(29.63, 105.83) * mm});
            skLineSegment(sketch, "E239.top", {"start": v(21.17, 97.37) * mm, "end": v(29.63, 97.37) * mm});
            skLineSegment(sketch, "E239.left", {"start": v(21.17, 105.83) * mm, "end": v(21.17, 97.37) * mm});
            skLineSegment(sketch, "E239.right", {"start": v(29.63, 105.83) * mm, "end": v(29.63, 97.37) * mm});
            skLineSegment(sketch, "E240.bottom", {"start": v(29.63, 80.43) * mm, "end": v(21.17, 80.43) * mm});
            skLineSegment(sketch, "E240.top", {"start": v(29.63, 71.97) * mm, "end": v(21.17, 71.97) * mm});
            skLineSegment(sketch, "E240.left", {"start": v(29.63, 80.43) * mm, "end": v(29.63, 71.97) * mm});
            skLineSegment(sketch, "E240.right", {"start": v(21.17, 80.43) * mm, "end": v(21.17, 71.97) * mm});
            skLineSegment(sketch, "E241.bottom", {"start": v(21.17, 55.03) * mm, "end": v(29.63, 55.03) * mm});
            skLineSegment(sketch, "E241.top", {"start": v(21.17, 46.57) * mm, "end": v(29.63, 46.57) * mm});
            skLineSegment(sketch, "E241.left", {"start": v(21.17, 55.03) * mm, "end": v(21.17, 46.57) * mm});
            skLineSegment(sketch, "E241.right", {"start": v(29.63, 55.03) * mm, "end": v(29.63, 46.57) * mm});
            skLineSegment(sketch, "E242.bottom", {"start": v(4.23, 55.03) * mm, "end": v(-4.23, 55.03) * mm});
            skLineSegment(sketch, "E242.top", {"start": v(4.23, 46.57) * mm, "end": v(-4.23, 46.57) * mm});
            skLineSegment(sketch, "E242.left", {"start": v(4.23, 55.03) * mm, "end": v(4.23, 46.57) * mm});
            skLineSegment(sketch, "E242.right", {"start": v(-4.23, 55.03) * mm, "end": v(-4.23, 46.57) * mm});
            skLineSegment(sketch, "E243.bottom", {"start": v(-21.17, 55.03) * mm, "end": v(-29.63, 55.03) * mm});
            skLineSegment(sketch, "E243.top", {"start": v(-21.17, 46.57) * mm, "end": v(-29.63, 46.57) * mm});
            skLineSegment(sketch, "E243.left", {"start": v(-21.17, 55.03) * mm, "end": v(-21.17, 46.57) * mm});
            skLineSegment(sketch, "E243.right", {"start": v(-29.63, 55.03) * mm, "end": v(-29.63, 46.57) * mm});
            skLineSegment(sketch, "E244.bottom", {"start": v(-21.17, 80.43) * mm, "end": v(-29.63, 80.43) * mm});
            skLineSegment(sketch, "E244.top", {"start": v(-21.17, 71.97) * mm, "end": v(-29.63, 71.97) * mm});
            skLineSegment(sketch, "E244.left", {"start": v(-21.17, 80.43) * mm, "end": v(-21.17, 71.97) * mm});
            skLineSegment(sketch, "E244.right", {"start": v(-29.63, 80.43) * mm, "end": v(-29.63, 71.97) * mm});
            skLineSegment(sketch, "E245", {"start": v(-114.3, 0) * mm, "end": v(114.3, 0) * mm, "construction": true});
            skPoint(sketch, "E246.MirrorP", {"position": v(-25.4, -101.6) * mm});
            skPoint(sketch, "E247.MirrorP", {"position": v(0, -101.6) * mm});
            skLineSegment(sketch, "E248.MirrorCS", {"start": v(21.17, -97.37) * mm, "end": v(29.63, -97.37) * mm});
            skPoint(sketch, "E249.MirrorP", {"position": v(-25.4, -76.2) * mm});
            skPoint(sketch, "E250.MirrorP", {"position": v(-25.4, -50.8) * mm});
            skPoint(sketch, "E251.MirrorP", {"position": v(25.4, -101.6) * mm});
            skPoint(sketch, "E252.MirrorP", {"position": v(0, -50.8) * mm});
            skPoint(sketch, "E253.MirrorP", {"position": v(25.4, -76.2) * mm});
            skPoint(sketch, "E254.MirrorP", {"position": v(25.4, -50.8) * mm});
            skPoint(sketch, "E255.MirrorP", {"position": v(0, -76.2) * mm});
            skLineSegment(sketch, "E256.MirrorCS", {"start": v(4.23, -55.03) * mm, "end": v(4.23, -46.57) * mm});
            skLineSegment(sketch, "E257.MirrorCS", {"start": v(-21.17, -71.97) * mm, "end": v(-29.63, -71.97) * mm});
            skLineSegment(sketch, "E258.MirrorCS", {"start": v(-21.17, -55.03) * mm, "end": v(-21.17, -46.57) * mm});
            skLineSegment(sketch, "E259.MirrorCS", {"start": v(21.17, -80.43) * mm, "end": v(21.17, -71.97) * mm});
            skLineSegment(sketch, "E260.MirrorCS", {"start": v(-4.23, -55.03) * mm, "end": v(-4.23, -46.57) * mm});
            skLineSegment(sketch, "E261.MirrorCS", {"start": v(-21.17, -97.37) * mm, "end": v(-29.63, -97.37) * mm});
            skLineSegment(sketch, "E262.MirrorCS", {"start": v(4.23, -46.57) * mm, "end": v(-4.23, -46.57) * mm});
            skLineSegment(sketch, "E263.MirrorCS", {"start": v(-29.63, -80.43) * mm, "end": v(-29.63, -71.97) * mm});
            skLineSegment(sketch, "E264.MirrorCS", {"start": v(-21.17, -105.83) * mm, "end": v(-21.17, -97.37) * mm});
            skLineSegment(sketch, "E265.MirrorCS", {"start": v(-21.17, -80.43) * mm, "end": v(-29.63, -80.43) * mm});
            skLineSegment(sketch, "E266.MirrorCS", {"start": v(-4.23, -105.83) * mm, "end": v(-4.23, -97.37) * mm});
            skLineSegment(sketch, "E267.MirrorCS", {"start": v(4.23, -97.37) * mm, "end": v(-4.23, -97.37) * mm});
            skLineSegment(sketch, "E268.MirrorCS", {"start": v(29.63, -71.97) * mm, "end": v(21.17, -71.97) * mm});
            skLineSegment(sketch, "E269.MirrorCS", {"start": v(21.17, -105.83) * mm, "end": v(29.63, -105.83) * mm});
            skLineSegment(sketch, "E270.MirrorCS", {"start": v(-21.17, -46.57) * mm, "end": v(-29.63, -46.57) * mm});
            skLineSegment(sketch, "E271.MirrorCS", {"start": v(21.17, -105.83) * mm, "end": v(21.17, -97.37) * mm});
            skLineSegment(sketch, "E272.MirrorCS", {"start": v(29.63, -80.43) * mm, "end": v(29.63, -71.97) * mm});
            skLineSegment(sketch, "E273.MirrorCS", {"start": v(29.63, -80.43) * mm, "end": v(21.17, -80.43) * mm});
            skLineSegment(sketch, "E274.MirrorCS", {"start": v(21.17, -55.03) * mm, "end": v(29.63, -55.03) * mm});
            skLineSegment(sketch, "E275.MirrorCS", {"start": v(21.17, -55.03) * mm, "end": v(21.17, -46.57) * mm});
            skLineSegment(sketch, "E276.MirrorCS", {"start": v(-29.63, -55.03) * mm, "end": v(-29.63, -46.57) * mm});
            skLineSegment(sketch, "E277.MirrorCS", {"start": v(4.23, -55.03) * mm, "end": v(-4.23, -55.03) * mm});
            skLineSegment(sketch, "E278.MirrorCS", {"start": v(4.23, -105.83) * mm, "end": v(4.23, -97.37) * mm});
            skLineSegment(sketch, "E279.MirrorCS", {"start": v(29.63, -105.83) * mm, "end": v(29.63, -97.37) * mm});
            skLineSegment(sketch, "E280.MirrorCS", {"start": v(4.23, -105.83) * mm, "end": v(-4.23, -105.83) * mm});
            skLineSegment(sketch, "E281.MirrorCS", {"start": v(-21.17, -80.43) * mm, "end": v(-21.17, -71.97) * mm});
            skLineSegment(sketch, "E282.MirrorCS", {"start": v(-21.17, -55.03) * mm, "end": v(-29.63, -55.03) * mm});
            skLineSegment(sketch, "E283.MirrorCS", {"start": v(-21.17, -105.83) * mm, "end": v(-29.63, -105.83) * mm});
            skLineSegment(sketch, "E284.MirrorCS", {"start": v(-29.63, -105.83) * mm, "end": v(-29.63, -97.37) * mm});
            skLineSegment(sketch, "E285.MirrorCS", {"start": v(29.63, -55.03) * mm, "end": v(29.63, -46.57) * mm});
            skLineSegment(sketch, "E286.MirrorCS", {"start": v(21.17, -46.57) * mm, "end": v(29.63, -46.57) * mm});
            skSolve(sketch);
        }
        {
            var Q0;
            Q0 = qSketchRegion(id + "F11", true);
            extrude(context, id + "F12", {"entities" : qUnion([Q0]), "operationType" : NewBodyOperationType.REMOVE, "oppositeDirection" : true, "depth" : 228.6 * mm, "offsetDistance" : 25.4 * mm});
        }
        {
            var Q0;
            {var subQ0=sQuery(id+"F0.wireOp",EDGE,"E0.left");Q0=makeQuery(id+"F8.imprint","IMPRINT",FACE,{"disambiguationData":[TD([[makeQuery(id+"F8.imprint","IMPRINT",EDGE,{"derivedFrom":makeQuery(id+"F1.opExtrude","CAP_EDGE",EDGE,{"disambiguationData":[OSD([subQ0])],"isStart":true})}),-1.0]])]});}
            var sketch = newSketch(context, id + "F13", { "sketchPlane" : qUnion([Q0])});
            skPoint(sketch, "E287", {"position": v(0, 76.2) * mm});
            skPoint(sketch, "E288", {"position": v(76.2, 0) * mm});
            skPoint(sketch, "E289", {"position": v(0, -76.2) * mm});
            skPoint(sketch, "E290", {"position": v(-76.2, 0) * mm});
            skLineSegment(sketch, "E291.bottom", {"start": v(12.7, 88.9) * mm, "end": v(-12.7, 88.9) * mm});
            skLineSegment(sketch, "E291.top", {"start": v(12.7, 63.5) * mm, "end": v(-12.7, 63.5) * mm});
            skLineSegment(sketch, "E291.left", {"start": v(12.7, 88.9) * mm, "end": v(12.7, 63.5) * mm});
            skLineSegment(sketch, "E291.right", {"start": v(-12.7, 88.9) * mm, "end": v(-12.7, 63.5) * mm});
            skLineSegment(sketch, "E292.bottom", {"start": v(88.9, 12.7) * mm, "end": v(63.5, 12.7) * mm});
            skLineSegment(sketch, "E292.top", {"start": v(88.9, -12.7) * mm, "end": v(63.5, -12.7) * mm});
            skLineSegment(sketch, "E292.left", {"start": v(88.9, 12.7) * mm, "end": v(88.9, -12.7) * mm});
            skLineSegment(sketch, "E292.right", {"start": v(63.5, 12.7) * mm, "end": v(63.5, -12.7) * mm});
            skLineSegment(sketch, "E293.bottom", {"start": v(12.7, -63.5) * mm, "end": v(-12.7, -63.5) * mm});
            skLineSegment(sketch, "E293.top", {"start": v(12.7, -88.9) * mm, "end": v(-12.7, -88.9) * mm});
            skLineSegment(sketch, "E293.left", {"start": v(12.7, -63.5) * mm, "end": v(12.7, -88.9) * mm});
            skLineSegment(sketch, "E293.right", {"start": v(-12.7, -63.5) * mm, "end": v(-12.7, -88.9) * mm});
            skLineSegment(sketch, "E294.bottom", {"start": v(-63.5, 12.7) * mm, "end": v(-88.9, 12.7) * mm});
            skLineSegment(sketch, "E294.top", {"start": v(-63.5, -12.7) * mm, "end": v(-88.9, -12.7) * mm});
            skLineSegment(sketch, "E294.left", {"start": v(-63.5, 12.7) * mm, "end": v(-63.5, -12.7) * mm});
            skLineSegment(sketch, "E294.right", {"start": v(-88.9, 12.7) * mm, "end": v(-88.9, -12.7) * mm});
            skPoint(sketch, "E295", {"position": v(-76.2, 76.2) * mm});
            skLineSegment(sketch, "E296.bottom", {"start": v(-88.9, 88.9) * mm, "end": v(-63.5, 88.9) * mm});
            skLineSegment(sketch, "E296.top", {"start": v(-88.9, 63.5) * mm, "end": v(-63.5, 63.5) * mm});
            skLineSegment(sketch, "E296.left", {"start": v(-88.9, 88.9) * mm, "end": v(-88.9, 63.5) * mm});
            skLineSegment(sketch, "E296.right", {"start": v(-63.5, 88.9) * mm, "end": v(-63.5, 63.5) * mm});
            skPoint(sketch, "E297", {"position": v(76.2, 76.2) * mm});
            skPoint(sketch, "E297.positionSnap0", {"position": v(12.7, 76.2) * mm});
            skLineSegment(sketch, "E298.bottom", {"start": v(88.9, 88.9) * mm, "end": v(63.5, 88.9) * mm});
            skLineSegment(sketch, "E298.top", {"start": v(88.9, 63.5) * mm, "end": v(63.5, 63.5) * mm});
            skLineSegment(sketch, "E298.left", {"start": v(88.9, 88.9) * mm, "end": v(88.9, 63.5) * mm});
            skLineSegment(sketch, "E298.right", {"start": v(63.5, 88.9) * mm, "end": v(63.5, 63.5) * mm});
            skPoint(sketch, "E299", {"position": v(76.2, -76.2) * mm});
            skLineSegment(sketch, "E300.bottom", {"start": v(88.9, -63.5) * mm, "end": v(63.5, -63.5) * mm});
            skLineSegment(sketch, "E300.top", {"start": v(88.9, -88.9) * mm, "end": v(63.5, -88.9) * mm});
            skLineSegment(sketch, "E300.left", {"start": v(88.9, -63.5) * mm, "end": v(88.9, -88.9) * mm});
            skLineSegment(sketch, "E300.right", {"start": v(63.5, -63.5) * mm, "end": v(63.5, -88.9) * mm});
            skPoint(sketch, "E301", {"position": v(-76.2, -76.2) * mm});
            skLineSegment(sketch, "E302.bottom", {"start": v(-63.5, -63.5) * mm, "end": v(-88.9, -63.5) * mm});
            skLineSegment(sketch, "E302.top", {"start": v(-63.5, -88.9) * mm, "end": v(-88.9, -88.9) * mm});
            skLineSegment(sketch, "E302.left", {"start": v(-63.5, -63.5) * mm, "end": v(-63.5, -88.9) * mm});
            skLineSegment(sketch, "E302.right", {"start": v(-88.9, -63.5) * mm, "end": v(-88.9, -88.9) * mm});
            skPoint(sketch, "E303", {"position": v(-50.8, 76.2) * mm});
            skPoint(sketch, "E304", {"position": v(-76.2, 101.6) * mm});
            skPoint(sketch, "E305", {"position": v(-101.6, 76.2) * mm});
            skPoint(sketch, "E306", {"position": v(-76.2, 50.8) * mm});
            skPoint(sketch, "E306.positionSnap0", {"position": v(-76.2, 63.5) * mm});
            skPoint(sketch, "E307", {"position": v(-101.6, 101.6) * mm});
            skPoint(sketch, "E308", {"position": v(-50.8, 101.6) * mm});
            skPoint(sketch, "E309", {"position": v(-50.8, 50.8) * mm});
            skPoint(sketch, "E310", {"position": v(-101.6, 50.8) * mm});
            skLineSegment(sketch, "E311.bottom", {"start": v(-97.37, 105.83) * mm, "end": v(-105.83, 105.83) * mm});
            skLineSegment(sketch, "E311.top", {"start": v(-97.37, 97.37) * mm, "end": v(-105.83, 97.37) * mm});
            skLineSegment(sketch, "E311.left", {"start": v(-97.37, 105.83) * mm, "end": v(-97.37, 97.37) * mm});
            skLineSegment(sketch, "E311.right", {"start": v(-105.83, 105.83) * mm, "end": v(-105.83, 97.37) * mm});
            skLineSegment(sketch, "E312.bottom", {"start": v(-71.97, 105.83) * mm, "end": v(-80.43, 105.83) * mm});
            skLineSegment(sketch, "E312.top", {"start": v(-71.97, 97.37) * mm, "end": v(-80.43, 97.37) * mm});
            skLineSegment(sketch, "E312.left", {"start": v(-71.97, 105.83) * mm, "end": v(-71.97, 97.37) * mm});
            skLineSegment(sketch, "E312.right", {"start": v(-80.43, 105.83) * mm, "end": v(-80.43, 97.37) * mm});
            skLineSegment(sketch, "E313.bottom", {"start": v(-55.03, 105.83) * mm, "end": v(-46.57, 105.83) * mm});
            skLineSegment(sketch, "E313.top", {"start": v(-55.03, 97.37) * mm, "end": v(-46.57, 97.37) * mm});
            skLineSegment(sketch, "E313.left", {"start": v(-55.03, 105.83) * mm, "end": v(-55.03, 97.37) * mm});
            skLineSegment(sketch, "E313.right", {"start": v(-46.57, 105.83) * mm, "end": v(-46.57, 97.37) * mm});
            skLineSegment(sketch, "E314.bottom", {"start": v(-46.57, 80.43) * mm, "end": v(-55.03, 80.43) * mm});
            skLineSegment(sketch, "E314.top", {"start": v(-46.57, 71.97) * mm, "end": v(-55.03, 71.97) * mm});
            skLineSegment(sketch, "E314.left", {"start": v(-46.57, 80.43) * mm, "end": v(-46.57, 71.97) * mm});
            skLineSegment(sketch, "E314.right", {"start": v(-55.03, 80.43) * mm, "end": v(-55.03, 71.97) * mm});
            skLineSegment(sketch, "E315.bottom", {"start": v(-71.97, 55.03) * mm, "end": v(-80.43, 55.03) * mm});
            skLineSegment(sketch, "E315.top", {"start": v(-71.97, 46.57) * mm, "end": v(-80.43, 46.57) * mm});
            skLineSegment(sketch, "E315.left", {"start": v(-71.97, 55.03) * mm, "end": v(-71.97, 46.57) * mm});
            skLineSegment(sketch, "E315.right", {"start": v(-80.43, 55.03) * mm, "end": v(-80.43, 46.57) * mm});
            skLineSegment(sketch, "E316.bottom", {"start": v(-46.57, 55.03) * mm, "end": v(-55.03, 55.03) * mm});
            skLineSegment(sketch, "E316.top", {"start": v(-46.57, 46.57) * mm, "end": v(-55.03, 46.57) * mm});
            skLineSegment(sketch, "E316.left", {"start": v(-46.57, 55.03) * mm, "end": v(-46.57, 46.57) * mm});
            skLineSegment(sketch, "E316.right", {"start": v(-55.03, 55.03) * mm, "end": v(-55.03, 46.57) * mm});
            skLineSegment(sketch, "E317.bottom", {"start": v(-97.37, 55.03) * mm, "end": v(-105.83, 55.03) * mm});
            skLineSegment(sketch, "E317.top", {"start": v(-97.37, 46.57) * mm, "end": v(-105.83, 46.57) * mm});
            skLineSegment(sketch, "E317.left", {"start": v(-97.37, 55.03) * mm, "end": v(-97.37, 46.57) * mm});
            skLineSegment(sketch, "E317.right", {"start": v(-105.83, 55.03) * mm, "end": v(-105.83, 46.57) * mm});
            skLineSegment(sketch, "E318.bottom", {"start": v(-105.83, 80.43) * mm, "end": v(-97.37, 80.43) * mm});
            skLineSegment(sketch, "E318.top", {"start": v(-105.83, 71.97) * mm, "end": v(-97.37, 71.97) * mm});
            skLineSegment(sketch, "E318.left", {"start": v(-105.83, 80.43) * mm, "end": v(-105.83, 71.97) * mm});
            skLineSegment(sketch, "E318.right", {"start": v(-97.37, 80.43) * mm, "end": v(-97.37, 71.97) * mm});
            skLineSegment(sketch, "E319.0.1.0", {"start": v(-97.37, 21.17) * mm, "end": v(-105.83, 21.17) * mm});
            skLineSegment(sketch, "E319.0.1.1", {"start": v(-105.83, -4.23) * mm, "end": v(-97.37, -4.23) * mm});
            skLineSegment(sketch, "E319.0.1.2", {"start": v(-46.57, -29.63) * mm, "end": v(-55.03, -29.63) * mm});
            skPoint(sketch, "E319.0.1.3", {"position": v(-101.6, -25.4) * mm});
            skPoint(sketch, "E319.0.1.4", {"position": v(-50.8, 0) * mm});
            skLineSegment(sketch, "E319.0.1.5", {"start": v(-105.83, 4.23) * mm, "end": v(-97.37, 4.23) * mm});
            skPoint(sketch, "E319.0.1.6", {"position": v(-76.2, 25.4) * mm});
            skLineSegment(sketch, "E319.0.1.7", {"start": v(-46.57, -21.17) * mm, "end": v(-55.03, -21.17) * mm});
            skLineSegment(sketch, "E319.0.1.8", {"start": v(-55.03, 29.63) * mm, "end": v(-46.57, 29.63) * mm});
            skLineSegment(sketch, "E319.0.1.9", {"start": v(-46.57, -4.23) * mm, "end": v(-55.03, -4.23) * mm});
            skLineSegment(sketch, "E319.0.1.10", {"start": v(-105.83, 29.63) * mm, "end": v(-105.83, 21.17) * mm});
            skLineSegment(sketch, "E319.0.1.11", {"start": v(-97.37, -21.17) * mm, "end": v(-97.37, -29.63) * mm});
            skLineSegment(sketch, "E319.0.1.12", {"start": v(-71.97, 29.63) * mm, "end": v(-71.97, 21.17) * mm});
            skLineSegment(sketch, "E319.0.1.13", {"start": v(-97.37, 29.63) * mm, "end": v(-105.83, 29.63) * mm});
            skLineSegment(sketch, "E319.0.1.14", {"start": v(-55.03, 21.17) * mm, "end": v(-46.57, 21.17) * mm});
            skPoint(sketch, "E319.0.1.15", {"position": v(-76.2, -25.4) * mm});
            skLineSegment(sketch, "E319.0.1.16", {"start": v(-71.97, 21.17) * mm, "end": v(-80.43, 21.17) * mm});
            skPoint(sketch, "E319.0.1.17", {"position": v(-50.8, -25.4) * mm});
            skLineSegment(sketch, "E319.0.1.18", {"start": v(-97.37, -29.63) * mm, "end": v(-105.83, -29.63) * mm});
            skLineSegment(sketch, "E319.0.1.19", {"start": v(-71.97, -21.17) * mm, "end": v(-71.97, -29.63) * mm});
            skLineSegment(sketch, "E319.0.1.20", {"start": v(-46.57, 4.23) * mm, "end": v(-55.03, 4.23) * mm});
            skLineSegment(sketch, "E319.0.1.21", {"start": v(-105.83, -21.17) * mm, "end": v(-105.83, -29.63) * mm});
            skLineSegment(sketch, "E319.0.1.22", {"start": v(-46.57, 29.63) * mm, "end": v(-46.57, 21.17) * mm});
            skLineSegment(sketch, "E319.0.1.23", {"start": v(-71.97, 29.63) * mm, "end": v(-80.43, 29.63) * mm});
            skLineSegment(sketch, "E319.0.1.24", {"start": v(-97.37, 29.63) * mm, "end": v(-97.37, 21.17) * mm});
            skLineSegment(sketch, "E319.0.1.25", {"start": v(-105.83, 4.23) * mm, "end": v(-105.83, -4.23) * mm});
            skPoint(sketch, "E319.0.1.26", {"position": v(-101.6, 0) * mm});
            skPoint(sketch, "E319.0.1.27", {"position": v(-50.8, 25.4) * mm});
            skPoint(sketch, "E319.0.1.28", {"position": v(-101.6, 25.4) * mm});
            skLineSegment(sketch, "E319.0.1.29", {"start": v(-46.57, -21.17) * mm, "end": v(-46.57, -29.63) * mm});
            skLineSegment(sketch, "E319.0.1.30", {"start": v(-46.57, 4.23) * mm, "end": v(-46.57, -4.23) * mm});
            skLineSegment(sketch, "E319.0.1.31", {"start": v(-97.37, -21.17) * mm, "end": v(-105.83, -21.17) * mm});
            skPoint(sketch, "E319.0.1.32", {"position": v(-50.8, -25.4) * mm});
            skLineSegment(sketch, "E319.0.1.33", {"start": v(-71.97, -21.17) * mm, "end": v(-80.43, -21.17) * mm});
            skLineSegment(sketch, "E319.0.1.34", {"start": v(-80.43, 29.63) * mm, "end": v(-80.43, 21.17) * mm});
            skPoint(sketch, "E319.0.1.35", {"position": v(-50.8, 25.4) * mm});
            skLineSegment(sketch, "E319.0.1.36", {"start": v(-97.37, 4.23) * mm, "end": v(-97.37, -4.23) * mm});
            skLineSegment(sketch, "E319.0.1.37", {"start": v(-55.03, -21.17) * mm, "end": v(-55.03, -29.63) * mm});
            skPoint(sketch, "E319.0.1.38", {"position": v(-76.2, 25.4) * mm});
            skPoint(sketch, "E319.0.1.39", {"position": v(-50.8, 0) * mm});
            skPoint(sketch, "E319.0.1.40", {"position": v(-101.6, -25.4) * mm});
            skPoint(sketch, "E319.0.1.41", {"position": v(-76.2, -25.4) * mm});
            skLineSegment(sketch, "E319.0.1.42", {"start": v(-71.97, -29.63) * mm, "end": v(-80.43, -29.63) * mm});
            skPoint(sketch, "E319.0.1.44", {"position": v(-101.6, 25.4) * mm});
            skLineSegment(sketch, "E319.0.1.45", {"start": v(-55.03, 29.63) * mm, "end": v(-55.03, 21.17) * mm});
            skPoint(sketch, "E319.0.1.46", {"position": v(-101.6, 0) * mm});
            skLineSegment(sketch, "E319.0.1.47", {"start": v(-55.03, 4.23) * mm, "end": v(-55.03, -4.23) * mm});
            skLineSegment(sketch, "E319.0.1.48", {"start": v(-80.43, -21.17) * mm, "end": v(-80.43, -29.63) * mm});
            skPoint(sketch, "E319.0.1.49", {"position": v(-50.8, -25.4) * mm});
            skLineSegment(sketch, "E319.0.2.0", {"start": v(-97.37, -55.03) * mm, "end": v(-105.83, -55.03) * mm});
            skLineSegment(sketch, "E319.0.2.1", {"start": v(-105.83, -80.43) * mm, "end": v(-97.37, -80.43) * mm});
            skLineSegment(sketch, "E319.0.2.2", {"start": v(-46.57, -105.83) * mm, "end": v(-55.03, -105.83) * mm});
            skPoint(sketch, "E319.0.2.3", {"position": v(-101.6, -101.6) * mm});
            skPoint(sketch, "E319.0.2.4", {"position": v(-50.8, -76.2) * mm});
            skLineSegment(sketch, "E319.0.2.5", {"start": v(-105.83, -71.97) * mm, "end": v(-97.37, -71.97) * mm});
            skPoint(sketch, "E319.0.2.6", {"position": v(-76.2, -50.8) * mm});
            skLineSegment(sketch, "E319.0.2.7", {"start": v(-46.57, -97.37) * mm, "end": v(-55.03, -97.37) * mm});
            skLineSegment(sketch, "E319.0.2.8", {"start": v(-55.03, -46.57) * mm, "end": v(-46.57, -46.57) * mm});
            skLineSegment(sketch, "E319.0.2.9", {"start": v(-46.57, -80.43) * mm, "end": v(-55.03, -80.43) * mm});
            skLineSegment(sketch, "E319.0.2.10", {"start": v(-105.83, -46.57) * mm, "end": v(-105.83, -55.03) * mm});
            skLineSegment(sketch, "E319.0.2.11", {"start": v(-97.37, -97.37) * mm, "end": v(-97.37, -105.83) * mm});
            skLineSegment(sketch, "E319.0.2.12", {"start": v(-71.97, -46.57) * mm, "end": v(-71.97, -55.03) * mm});
            skLineSegment(sketch, "E319.0.2.13", {"start": v(-97.37, -46.57) * mm, "end": v(-105.83, -46.57) * mm});
            skLineSegment(sketch, "E319.0.2.14", {"start": v(-55.03, -55.03) * mm, "end": v(-46.57, -55.03) * mm});
            skPoint(sketch, "E319.0.2.15", {"position": v(-76.2, -101.6) * mm});
            skLineSegment(sketch, "E319.0.2.16", {"start": v(-71.97, -55.03) * mm, "end": v(-80.43, -55.03) * mm});
            skPoint(sketch, "E319.0.2.17", {"position": v(-50.8, -101.6) * mm});
            skLineSegment(sketch, "E319.0.2.18", {"start": v(-97.37, -105.83) * mm, "end": v(-105.83, -105.83) * mm});
            skLineSegment(sketch, "E319.0.2.19", {"start": v(-71.97, -97.37) * mm, "end": v(-71.97, -105.83) * mm});
            skLineSegment(sketch, "E319.0.2.20", {"start": v(-46.57, -71.97) * mm, "end": v(-55.03, -71.97) * mm});
            skLineSegment(sketch, "E319.0.2.21", {"start": v(-105.83, -97.37) * mm, "end": v(-105.83, -105.83) * mm});
            skLineSegment(sketch, "E319.0.2.22", {"start": v(-46.57, -46.57) * mm, "end": v(-46.57, -55.03) * mm});
            skLineSegment(sketch, "E319.0.2.23", {"start": v(-71.97, -46.57) * mm, "end": v(-80.43, -46.57) * mm});
            skLineSegment(sketch, "E319.0.2.24", {"start": v(-97.37, -46.57) * mm, "end": v(-97.37, -55.03) * mm});
            skLineSegment(sketch, "E319.0.2.25", {"start": v(-105.83, -71.97) * mm, "end": v(-105.83, -80.43) * mm});
            skPoint(sketch, "E319.0.2.26", {"position": v(-101.6, -76.2) * mm});
            skPoint(sketch, "E319.0.2.27", {"position": v(-50.8, -50.8) * mm});
            skPoint(sketch, "E319.0.2.28", {"position": v(-101.6, -50.8) * mm});
            skLineSegment(sketch, "E319.0.2.29", {"start": v(-46.57, -97.37) * mm, "end": v(-46.57, -105.83) * mm});
            skLineSegment(sketch, "E319.0.2.30", {"start": v(-46.57, -71.97) * mm, "end": v(-46.57, -80.43) * mm});
            skLineSegment(sketch, "E319.0.2.31", {"start": v(-97.37, -97.37) * mm, "end": v(-105.83, -97.37) * mm});
            skPoint(sketch, "E319.0.2.32", {"position": v(-50.8, -101.6) * mm});
            skLineSegment(sketch, "E319.0.2.33", {"start": v(-71.97, -97.37) * mm, "end": v(-80.43, -97.37) * mm});
            skLineSegment(sketch, "E319.0.2.34", {"start": v(-80.43, -46.57) * mm, "end": v(-80.43, -55.03) * mm});
            skPoint(sketch, "E319.0.2.35", {"position": v(-50.8, -50.8) * mm});
            skLineSegment(sketch, "E319.0.2.36", {"start": v(-97.37, -71.97) * mm, "end": v(-97.37, -80.43) * mm});
            skLineSegment(sketch, "E319.0.2.37", {"start": v(-55.03, -97.37) * mm, "end": v(-55.03, -105.83) * mm});
            skPoint(sketch, "E319.0.2.38", {"position": v(-76.2, -50.8) * mm});
            skPoint(sketch, "E319.0.2.39", {"position": v(-50.8, -76.2) * mm});
            skPoint(sketch, "E319.0.2.40", {"position": v(-101.6, -101.6) * mm});
            skPoint(sketch, "E319.0.2.41", {"position": v(-76.2, -101.6) * mm});
            skLineSegment(sketch, "E319.0.2.42", {"start": v(-71.97, -105.83) * mm, "end": v(-80.43, -105.83) * mm});
            skPoint(sketch, "E319.0.2.44", {"position": v(-101.6, -50.8) * mm});
            skLineSegment(sketch, "E319.0.2.45", {"start": v(-55.03, -46.57) * mm, "end": v(-55.03, -55.03) * mm});
            skPoint(sketch, "E319.0.2.46", {"position": v(-101.6, -76.2) * mm});
            skLineSegment(sketch, "E319.0.2.47", {"start": v(-55.03, -71.97) * mm, "end": v(-55.03, -80.43) * mm});
            skLineSegment(sketch, "E319.0.2.48", {"start": v(-80.43, -97.37) * mm, "end": v(-80.43, -105.83) * mm});
            skPoint(sketch, "E319.0.2.49", {"position": v(-50.8, -101.6) * mm});
            skLineSegment(sketch, "E319.1.0.0", {"start": v(-21.17, 97.37) * mm, "end": v(-29.63, 97.37) * mm});
            skLineSegment(sketch, "E319.1.0.1", {"start": v(-29.63, 71.97) * mm, "end": v(-21.17, 71.97) * mm});
            skLineSegment(sketch, "E319.1.0.2", {"start": v(29.63, 46.57) * mm, "end": v(21.17, 46.57) * mm});
            skPoint(sketch, "E319.1.0.3", {"position": v(-25.4, 50.8) * mm});
            skPoint(sketch, "E319.1.0.4", {"position": v(25.4, 76.2) * mm});
            skLineSegment(sketch, "E319.1.0.5", {"start": v(-29.63, 80.43) * mm, "end": v(-21.17, 80.43) * mm});
            skPoint(sketch, "E319.1.0.6", {"position": v(0, 101.6) * mm});
            skLineSegment(sketch, "E319.1.0.7", {"start": v(29.63, 55.03) * mm, "end": v(21.17, 55.03) * mm});
            skLineSegment(sketch, "E319.1.0.8", {"start": v(21.17, 105.83) * mm, "end": v(29.63, 105.83) * mm});
            skLineSegment(sketch, "E319.1.0.9", {"start": v(29.63, 71.97) * mm, "end": v(21.17, 71.97) * mm});
            skLineSegment(sketch, "E319.1.0.10", {"start": v(-29.63, 105.83) * mm, "end": v(-29.63, 97.37) * mm});
            skLineSegment(sketch, "E319.1.0.11", {"start": v(-21.17, 55.03) * mm, "end": v(-21.17, 46.57) * mm});
            skLineSegment(sketch, "E319.1.0.12", {"start": v(4.23, 105.83) * mm, "end": v(4.23, 97.37) * mm});
            skLineSegment(sketch, "E319.1.0.13", {"start": v(-21.17, 105.83) * mm, "end": v(-29.63, 105.83) * mm});
            skLineSegment(sketch, "E319.1.0.14", {"start": v(21.17, 97.37) * mm, "end": v(29.63, 97.37) * mm});
            skPoint(sketch, "E319.1.0.15", {"position": v(0, 50.8) * mm});
            skLineSegment(sketch, "E319.1.0.16", {"start": v(4.23, 97.37) * mm, "end": v(-4.23, 97.37) * mm});
            skPoint(sketch, "E319.1.0.17", {"position": v(25.4, 50.8) * mm});
            skLineSegment(sketch, "E319.1.0.18", {"start": v(-21.17, 46.57) * mm, "end": v(-29.63, 46.57) * mm});
            skLineSegment(sketch, "E319.1.0.19", {"start": v(4.23, 55.03) * mm, "end": v(4.23, 46.57) * mm});
            skLineSegment(sketch, "E319.1.0.20", {"start": v(29.63, 80.43) * mm, "end": v(21.17, 80.43) * mm});
            skLineSegment(sketch, "E319.1.0.21", {"start": v(-29.63, 55.03) * mm, "end": v(-29.63, 46.57) * mm});
            skLineSegment(sketch, "E319.1.0.22", {"start": v(29.63, 105.83) * mm, "end": v(29.63, 97.37) * mm});
            skLineSegment(sketch, "E319.1.0.23", {"start": v(4.23, 105.83) * mm, "end": v(-4.23, 105.83) * mm});
            skLineSegment(sketch, "E319.1.0.24", {"start": v(-21.17, 105.83) * mm, "end": v(-21.17, 97.37) * mm});
            skLineSegment(sketch, "E319.1.0.25", {"start": v(-29.63, 80.43) * mm, "end": v(-29.63, 71.97) * mm});
            skPoint(sketch, "E319.1.0.26", {"position": v(-25.4, 76.2) * mm});
            skPoint(sketch, "E319.1.0.27", {"position": v(25.4, 101.6) * mm});
            skPoint(sketch, "E319.1.0.28", {"position": v(-25.4, 101.6) * mm});
            skLineSegment(sketch, "E319.1.0.29", {"start": v(29.63, 55.03) * mm, "end": v(29.63, 46.57) * mm});
            skLineSegment(sketch, "E319.1.0.30", {"start": v(29.63, 80.43) * mm, "end": v(29.63, 71.97) * mm});
            skLineSegment(sketch, "E319.1.0.31", {"start": v(-21.17, 55.03) * mm, "end": v(-29.63, 55.03) * mm});
            skPoint(sketch, "E319.1.0.32", {"position": v(25.4, 50.8) * mm});
            skLineSegment(sketch, "E319.1.0.33", {"start": v(4.23, 55.03) * mm, "end": v(-4.23, 55.03) * mm});
            skLineSegment(sketch, "E319.1.0.34", {"start": v(-4.23, 105.83) * mm, "end": v(-4.23, 97.37) * mm});
            skPoint(sketch, "E319.1.0.35", {"position": v(25.4, 101.6) * mm});
            skLineSegment(sketch, "E319.1.0.36", {"start": v(-21.17, 80.43) * mm, "end": v(-21.17, 71.97) * mm});
            skLineSegment(sketch, "E319.1.0.37", {"start": v(21.17, 55.03) * mm, "end": v(21.17, 46.57) * mm});
            skPoint(sketch, "E319.1.0.38", {"position": v(0, 101.6) * mm});
            skPoint(sketch, "E319.1.0.39", {"position": v(25.4, 76.2) * mm});
            skPoint(sketch, "E319.1.0.40", {"position": v(-25.4, 50.8) * mm});
            skPoint(sketch, "E319.1.0.41", {"position": v(0, 50.8) * mm});
            skLineSegment(sketch, "E319.1.0.42", {"start": v(4.23, 46.57) * mm, "end": v(-4.23, 46.57) * mm});
            skPoint(sketch, "E319.1.0.44", {"position": v(-25.4, 101.6) * mm});
            skLineSegment(sketch, "E319.1.0.45", {"start": v(21.17, 105.83) * mm, "end": v(21.17, 97.37) * mm});
            skPoint(sketch, "E319.1.0.46", {"position": v(-25.4, 76.2) * mm});
            skLineSegment(sketch, "E319.1.0.47", {"start": v(21.17, 80.43) * mm, "end": v(21.17, 71.97) * mm});
            skLineSegment(sketch, "E319.1.0.48", {"start": v(-4.23, 55.03) * mm, "end": v(-4.23, 46.57) * mm});
            skPoint(sketch, "E319.1.0.49", {"position": v(25.4, 50.8) * mm});
            skLineSegment(sketch, "E319.1.2.0", {"start": v(-21.17, -55.03) * mm, "end": v(-29.63, -55.03) * mm});
            skLineSegment(sketch, "E319.1.2.1", {"start": v(-29.63, -80.43) * mm, "end": v(-21.17, -80.43) * mm});
            skLineSegment(sketch, "E319.1.2.2", {"start": v(29.63, -105.83) * mm, "end": v(21.17, -105.83) * mm});
            skPoint(sketch, "E319.1.2.3", {"position": v(-25.4, -101.6) * mm});
            skPoint(sketch, "E319.1.2.4", {"position": v(25.4, -76.2) * mm});
            skLineSegment(sketch, "E319.1.2.5", {"start": v(-29.63, -71.97) * mm, "end": v(-21.17, -71.97) * mm});
            skPoint(sketch, "E319.1.2.6", {"position": v(0, -50.8) * mm});
            skLineSegment(sketch, "E319.1.2.7", {"start": v(29.63, -97.37) * mm, "end": v(21.17, -97.37) * mm});
            skLineSegment(sketch, "E319.1.2.8", {"start": v(21.17, -46.57) * mm, "end": v(29.63, -46.57) * mm});
            skLineSegment(sketch, "E319.1.2.9", {"start": v(29.63, -80.43) * mm, "end": v(21.17, -80.43) * mm});
            skLineSegment(sketch, "E319.1.2.10", {"start": v(-29.63, -46.57) * mm, "end": v(-29.63, -55.03) * mm});
            skLineSegment(sketch, "E319.1.2.11", {"start": v(-21.17, -97.37) * mm, "end": v(-21.17, -105.83) * mm});
            skLineSegment(sketch, "E319.1.2.12", {"start": v(4.23, -46.57) * mm, "end": v(4.23, -55.03) * mm});
            skLineSegment(sketch, "E319.1.2.13", {"start": v(-21.17, -46.57) * mm, "end": v(-29.63, -46.57) * mm});
            skLineSegment(sketch, "E319.1.2.14", {"start": v(21.17, -55.03) * mm, "end": v(29.63, -55.03) * mm});
            skPoint(sketch, "E319.1.2.15", {"position": v(0, -101.6) * mm});
            skLineSegment(sketch, "E319.1.2.16", {"start": v(4.23, -55.03) * mm, "end": v(-4.23, -55.03) * mm});
            skPoint(sketch, "E319.1.2.17", {"position": v(25.4, -101.6) * mm});
            skLineSegment(sketch, "E319.1.2.18", {"start": v(-21.17, -105.83) * mm, "end": v(-29.63, -105.83) * mm});
            skLineSegment(sketch, "E319.1.2.19", {"start": v(4.23, -97.37) * mm, "end": v(4.23, -105.83) * mm});
            skLineSegment(sketch, "E319.1.2.20", {"start": v(29.63, -71.97) * mm, "end": v(21.17, -71.97) * mm});
            skLineSegment(sketch, "E319.1.2.21", {"start": v(-29.63, -97.37) * mm, "end": v(-29.63, -105.83) * mm});
            skLineSegment(sketch, "E319.1.2.22", {"start": v(29.63, -46.57) * mm, "end": v(29.63, -55.03) * mm});
            skLineSegment(sketch, "E319.1.2.23", {"start": v(4.23, -46.57) * mm, "end": v(-4.23, -46.57) * mm});
            skLineSegment(sketch, "E319.1.2.24", {"start": v(-21.17, -46.57) * mm, "end": v(-21.17, -55.03) * mm});
            skLineSegment(sketch, "E319.1.2.25", {"start": v(-29.63, -71.97) * mm, "end": v(-29.63, -80.43) * mm});
            skPoint(sketch, "E319.1.2.26", {"position": v(-25.4, -76.2) * mm});
            skPoint(sketch, "E319.1.2.27", {"position": v(25.4, -50.8) * mm});
            skPoint(sketch, "E319.1.2.28", {"position": v(-25.4, -50.8) * mm});
            skLineSegment(sketch, "E319.1.2.29", {"start": v(29.63, -97.37) * mm, "end": v(29.63, -105.83) * mm});
            skLineSegment(sketch, "E319.1.2.30", {"start": v(29.63, -71.97) * mm, "end": v(29.63, -80.43) * mm});
            skLineSegment(sketch, "E319.1.2.31", {"start": v(-21.17, -97.37) * mm, "end": v(-29.63, -97.37) * mm});
            skPoint(sketch, "E319.1.2.32", {"position": v(25.4, -101.6) * mm});
            skLineSegment(sketch, "E319.1.2.33", {"start": v(4.23, -97.37) * mm, "end": v(-4.23, -97.37) * mm});
            skLineSegment(sketch, "E319.1.2.34", {"start": v(-4.23, -46.57) * mm, "end": v(-4.23, -55.03) * mm});
            skPoint(sketch, "E319.1.2.35", {"position": v(25.4, -50.8) * mm});
            skLineSegment(sketch, "E319.1.2.36", {"start": v(-21.17, -71.97) * mm, "end": v(-21.17, -80.43) * mm});
            skLineSegment(sketch, "E319.1.2.37", {"start": v(21.17, -97.37) * mm, "end": v(21.17, -105.83) * mm});
            skPoint(sketch, "E319.1.2.38", {"position": v(0, -50.8) * mm});
            skPoint(sketch, "E319.1.2.39", {"position": v(25.4, -76.2) * mm});
            skPoint(sketch, "E319.1.2.40", {"position": v(-25.4, -101.6) * mm});
            skPoint(sketch, "E319.1.2.41", {"position": v(0, -101.6) * mm});
            skLineSegment(sketch, "E319.1.2.42", {"start": v(4.23, -105.83) * mm, "end": v(-4.23, -105.83) * mm});
            skPoint(sketch, "E319.1.2.44", {"position": v(-25.4, -50.8) * mm});
            skLineSegment(sketch, "E319.1.2.45", {"start": v(21.17, -46.57) * mm, "end": v(21.17, -55.03) * mm});
            skPoint(sketch, "E319.1.2.46", {"position": v(-25.4, -76.2) * mm});
            skLineSegment(sketch, "E319.1.2.47", {"start": v(21.17, -71.97) * mm, "end": v(21.17, -80.43) * mm});
            skLineSegment(sketch, "E319.1.2.48", {"start": v(-4.23, -97.37) * mm, "end": v(-4.23, -105.83) * mm});
            skPoint(sketch, "E319.1.2.49", {"position": v(25.4, -101.6) * mm});
            skLineSegment(sketch, "E319.2.0.0", {"start": v(55.03, 97.37) * mm, "end": v(46.57, 97.37) * mm});
            skLineSegment(sketch, "E319.2.0.1", {"start": v(46.57, 71.97) * mm, "end": v(55.03, 71.97) * mm});
            skLineSegment(sketch, "E319.2.0.2", {"start": v(105.83, 46.57) * mm, "end": v(97.37, 46.57) * mm});
            skPoint(sketch, "E319.2.0.3", {"position": v(50.8, 50.8) * mm});
            skPoint(sketch, "E319.2.0.4", {"position": v(101.6, 76.2) * mm});
            skLineSegment(sketch, "E319.2.0.5", {"start": v(46.57, 80.43) * mm, "end": v(55.03, 80.43) * mm});
            skPoint(sketch, "E319.2.0.6", {"position": v(76.2, 101.6) * mm});
            skLineSegment(sketch, "E319.2.0.7", {"start": v(105.83, 55.03) * mm, "end": v(97.37, 55.03) * mm});
            skLineSegment(sketch, "E319.2.0.8", {"start": v(97.37, 105.83) * mm, "end": v(105.83, 105.83) * mm});
            skLineSegment(sketch, "E319.2.0.9", {"start": v(105.83, 71.97) * mm, "end": v(97.37, 71.97) * mm});
            skLineSegment(sketch, "E319.2.0.10", {"start": v(46.57, 105.83) * mm, "end": v(46.57, 97.37) * mm});
            skLineSegment(sketch, "E319.2.0.11", {"start": v(55.03, 55.03) * mm, "end": v(55.03, 46.57) * mm});
            skLineSegment(sketch, "E319.2.0.12", {"start": v(80.43, 105.83) * mm, "end": v(80.43, 97.37) * mm});
            skLineSegment(sketch, "E319.2.0.13", {"start": v(55.03, 105.83) * mm, "end": v(46.57, 105.83) * mm});
            skLineSegment(sketch, "E319.2.0.14", {"start": v(97.37, 97.37) * mm, "end": v(105.83, 97.37) * mm});
            skPoint(sketch, "E319.2.0.15", {"position": v(76.2, 50.8) * mm});
            skLineSegment(sketch, "E319.2.0.16", {"start": v(80.43, 97.37) * mm, "end": v(71.97, 97.37) * mm});
            skPoint(sketch, "E319.2.0.17", {"position": v(101.6, 50.8) * mm});
            skLineSegment(sketch, "E319.2.0.18", {"start": v(55.03, 46.57) * mm, "end": v(46.57, 46.57) * mm});
            skLineSegment(sketch, "E319.2.0.19", {"start": v(80.43, 55.03) * mm, "end": v(80.43, 46.57) * mm});
            skLineSegment(sketch, "E319.2.0.20", {"start": v(105.83, 80.43) * mm, "end": v(97.37, 80.43) * mm});
            skLineSegment(sketch, "E319.2.0.21", {"start": v(46.57, 55.03) * mm, "end": v(46.57, 46.57) * mm});
            skLineSegment(sketch, "E319.2.0.22", {"start": v(105.83, 105.83) * mm, "end": v(105.83, 97.37) * mm});
            skLineSegment(sketch, "E319.2.0.23", {"start": v(80.43, 105.83) * mm, "end": v(71.97, 105.83) * mm});
            skLineSegment(sketch, "E319.2.0.24", {"start": v(55.03, 105.83) * mm, "end": v(55.03, 97.37) * mm});
            skLineSegment(sketch, "E319.2.0.25", {"start": v(46.57, 80.43) * mm, "end": v(46.57, 71.97) * mm});
            skPoint(sketch, "E319.2.0.26", {"position": v(50.8, 76.2) * mm});
            skPoint(sketch, "E319.2.0.27", {"position": v(101.6, 101.6) * mm});
            skPoint(sketch, "E319.2.0.28", {"position": v(50.8, 101.6) * mm});
            skLineSegment(sketch, "E319.2.0.29", {"start": v(105.83, 55.03) * mm, "end": v(105.83, 46.57) * mm});
            skLineSegment(sketch, "E319.2.0.30", {"start": v(105.83, 80.43) * mm, "end": v(105.83, 71.97) * mm});
            skLineSegment(sketch, "E319.2.0.31", {"start": v(55.03, 55.03) * mm, "end": v(46.57, 55.03) * mm});
            skPoint(sketch, "E319.2.0.32", {"position": v(101.6, 50.8) * mm});
            skLineSegment(sketch, "E319.2.0.33", {"start": v(80.43, 55.03) * mm, "end": v(71.97, 55.03) * mm});
            skLineSegment(sketch, "E319.2.0.34", {"start": v(71.97, 105.83) * mm, "end": v(71.97, 97.37) * mm});
            skPoint(sketch, "E319.2.0.35", {"position": v(101.6, 101.6) * mm});
            skLineSegment(sketch, "E319.2.0.36", {"start": v(55.03, 80.43) * mm, "end": v(55.03, 71.97) * mm});
            skLineSegment(sketch, "E319.2.0.37", {"start": v(97.37, 55.03) * mm, "end": v(97.37, 46.57) * mm});
            skPoint(sketch, "E319.2.0.38", {"position": v(76.2, 101.6) * mm});
            skPoint(sketch, "E319.2.0.39", {"position": v(101.6, 76.2) * mm});
            skPoint(sketch, "E319.2.0.40", {"position": v(50.8, 50.8) * mm});
            skPoint(sketch, "E319.2.0.41", {"position": v(76.2, 50.8) * mm});
            skLineSegment(sketch, "E319.2.0.42", {"start": v(80.43, 46.57) * mm, "end": v(71.97, 46.57) * mm});
            skPoint(sketch, "E319.2.0.44", {"position": v(50.8, 101.6) * mm});
            skLineSegment(sketch, "E319.2.0.45", {"start": v(97.37, 105.83) * mm, "end": v(97.37, 97.37) * mm});
            skPoint(sketch, "E319.2.0.46", {"position": v(50.8, 76.2) * mm});
            skLineSegment(sketch, "E319.2.0.47", {"start": v(97.37, 80.43) * mm, "end": v(97.37, 71.97) * mm});
            skLineSegment(sketch, "E319.2.0.48", {"start": v(71.97, 55.03) * mm, "end": v(71.97, 46.57) * mm});
            skPoint(sketch, "E319.2.0.49", {"position": v(101.6, 50.8) * mm});
            skLineSegment(sketch, "E319.2.1.0", {"start": v(55.03, 21.17) * mm, "end": v(46.57, 21.17) * mm});
            skLineSegment(sketch, "E319.2.1.1", {"start": v(46.57, -4.23) * mm, "end": v(55.03, -4.23) * mm});
            skLineSegment(sketch, "E319.2.1.2", {"start": v(105.83, -29.63) * mm, "end": v(97.37, -29.63) * mm});
            skPoint(sketch, "E319.2.1.3", {"position": v(50.8, -25.4) * mm});
            skPoint(sketch, "E319.2.1.4", {"position": v(101.6, 0) * mm});
            skLineSegment(sketch, "E319.2.1.5", {"start": v(46.57, 4.23) * mm, "end": v(55.03, 4.23) * mm});
            skPoint(sketch, "E319.2.1.6", {"position": v(76.2, 25.4) * mm});
            skLineSegment(sketch, "E319.2.1.7", {"start": v(105.83, -21.17) * mm, "end": v(97.37, -21.17) * mm});
            skLineSegment(sketch, "E319.2.1.8", {"start": v(97.37, 29.63) * mm, "end": v(105.83, 29.63) * mm});
            skLineSegment(sketch, "E319.2.1.9", {"start": v(105.83, -4.23) * mm, "end": v(97.37, -4.23) * mm});
            skLineSegment(sketch, "E319.2.1.10", {"start": v(46.57, 29.63) * mm, "end": v(46.57, 21.17) * mm});
            skLineSegment(sketch, "E319.2.1.11", {"start": v(55.03, -21.17) * mm, "end": v(55.03, -29.63) * mm});
            skLineSegment(sketch, "E319.2.1.12", {"start": v(80.43, 29.63) * mm, "end": v(80.43, 21.17) * mm});
            skLineSegment(sketch, "E319.2.1.13", {"start": v(55.03, 29.63) * mm, "end": v(46.57, 29.63) * mm});
            skLineSegment(sketch, "E319.2.1.14", {"start": v(97.37, 21.17) * mm, "end": v(105.83, 21.17) * mm});
            skPoint(sketch, "E319.2.1.15", {"position": v(76.2, -25.4) * mm});
            skLineSegment(sketch, "E319.2.1.16", {"start": v(80.43, 21.17) * mm, "end": v(71.97, 21.17) * mm});
            skPoint(sketch, "E319.2.1.17", {"position": v(101.6, -25.4) * mm});
            skLineSegment(sketch, "E319.2.1.18", {"start": v(55.03, -29.63) * mm, "end": v(46.57, -29.63) * mm});
            skLineSegment(sketch, "E319.2.1.19", {"start": v(80.43, -21.17) * mm, "end": v(80.43, -29.63) * mm});
            skLineSegment(sketch, "E319.2.1.20", {"start": v(105.83, 4.23) * mm, "end": v(97.37, 4.23) * mm});
            skLineSegment(sketch, "E319.2.1.21", {"start": v(46.57, -21.17) * mm, "end": v(46.57, -29.63) * mm});
            skLineSegment(sketch, "E319.2.1.22", {"start": v(105.83, 29.63) * mm, "end": v(105.83, 21.17) * mm});
            skLineSegment(sketch, "E319.2.1.23", {"start": v(80.43, 29.63) * mm, "end": v(71.97, 29.63) * mm});
            skLineSegment(sketch, "E319.2.1.24", {"start": v(55.03, 29.63) * mm, "end": v(55.03, 21.17) * mm});
            skLineSegment(sketch, "E319.2.1.25", {"start": v(46.57, 4.23) * mm, "end": v(46.57, -4.23) * mm});
            skPoint(sketch, "E319.2.1.26", {"position": v(50.8, 0) * mm});
            skPoint(sketch, "E319.2.1.27", {"position": v(101.6, 25.4) * mm});
            skPoint(sketch, "E319.2.1.28", {"position": v(50.8, 25.4) * mm});
            skLineSegment(sketch, "E319.2.1.29", {"start": v(105.83, -21.17) * mm, "end": v(105.83, -29.63) * mm});
            skLineSegment(sketch, "E319.2.1.30", {"start": v(105.83, 4.23) * mm, "end": v(105.83, -4.23) * mm});
            skLineSegment(sketch, "E319.2.1.31", {"start": v(55.03, -21.17) * mm, "end": v(46.57, -21.17) * mm});
            skPoint(sketch, "E319.2.1.32", {"position": v(101.6, -25.4) * mm});
            skLineSegment(sketch, "E319.2.1.33", {"start": v(80.43, -21.17) * mm, "end": v(71.97, -21.17) * mm});
            skLineSegment(sketch, "E319.2.1.34", {"start": v(71.97, 29.63) * mm, "end": v(71.97, 21.17) * mm});
            skPoint(sketch, "E319.2.1.35", {"position": v(101.6, 25.4) * mm});
            skLineSegment(sketch, "E319.2.1.36", {"start": v(55.03, 4.23) * mm, "end": v(55.03, -4.23) * mm});
            skLineSegment(sketch, "E319.2.1.37", {"start": v(97.37, -21.17) * mm, "end": v(97.37, -29.63) * mm});
            skPoint(sketch, "E319.2.1.38", {"position": v(76.2, 25.4) * mm});
            skPoint(sketch, "E319.2.1.39", {"position": v(101.6, 0) * mm});
            skPoint(sketch, "E319.2.1.40", {"position": v(50.8, -25.4) * mm});
            skPoint(sketch, "E319.2.1.41", {"position": v(76.2, -25.4) * mm});
            skLineSegment(sketch, "E319.2.1.42", {"start": v(80.43, -29.63) * mm, "end": v(71.97, -29.63) * mm});
            skPoint(sketch, "E319.2.1.44", {"position": v(50.8, 25.4) * mm});
            skLineSegment(sketch, "E319.2.1.45", {"start": v(97.37, 29.63) * mm, "end": v(97.37, 21.17) * mm});
            skPoint(sketch, "E319.2.1.46", {"position": v(50.8, 0) * mm});
            skLineSegment(sketch, "E319.2.1.47", {"start": v(97.37, 4.23) * mm, "end": v(97.37, -4.23) * mm});
            skLineSegment(sketch, "E319.2.1.48", {"start": v(71.97, -21.17) * mm, "end": v(71.97, -29.63) * mm});
            skPoint(sketch, "E319.2.1.49", {"position": v(101.6, -25.4) * mm});
            skLineSegment(sketch, "E319.2.2.0", {"start": v(55.03, -55.03) * mm, "end": v(46.57, -55.03) * mm});
            skLineSegment(sketch, "E319.2.2.1", {"start": v(46.57, -80.43) * mm, "end": v(55.03, -80.43) * mm});
            skLineSegment(sketch, "E319.2.2.2", {"start": v(105.83, -105.83) * mm, "end": v(97.37, -105.83) * mm});
            skPoint(sketch, "E319.2.2.3", {"position": v(50.8, -101.6) * mm});
            skPoint(sketch, "E319.2.2.4", {"position": v(101.6, -76.2) * mm});
            skLineSegment(sketch, "E319.2.2.5", {"start": v(46.57, -71.97) * mm, "end": v(55.03, -71.97) * mm});
            skPoint(sketch, "E319.2.2.6", {"position": v(76.2, -50.8) * mm});
            skLineSegment(sketch, "E319.2.2.7", {"start": v(105.83, -97.37) * mm, "end": v(97.37, -97.37) * mm});
            skLineSegment(sketch, "E319.2.2.8", {"start": v(97.37, -46.57) * mm, "end": v(105.83, -46.57) * mm});
            skLineSegment(sketch, "E319.2.2.9", {"start": v(105.83, -80.43) * mm, "end": v(97.37, -80.43) * mm});
            skLineSegment(sketch, "E319.2.2.10", {"start": v(46.57, -46.57) * mm, "end": v(46.57, -55.03) * mm});
            skLineSegment(sketch, "E319.2.2.11", {"start": v(55.03, -97.37) * mm, "end": v(55.03, -105.83) * mm});
            skLineSegment(sketch, "E319.2.2.12", {"start": v(80.43, -46.57) * mm, "end": v(80.43, -55.03) * mm});
            skLineSegment(sketch, "E319.2.2.13", {"start": v(55.03, -46.57) * mm, "end": v(46.57, -46.57) * mm});
            skLineSegment(sketch, "E319.2.2.14", {"start": v(97.37, -55.03) * mm, "end": v(105.83, -55.03) * mm});
            skPoint(sketch, "E319.2.2.15", {"position": v(76.2, -101.6) * mm});
            skLineSegment(sketch, "E319.2.2.16", {"start": v(80.43, -55.03) * mm, "end": v(71.97, -55.03) * mm});
            skPoint(sketch, "E319.2.2.17", {"position": v(101.6, -101.6) * mm});
            skLineSegment(sketch, "E319.2.2.18", {"start": v(55.03, -105.83) * mm, "end": v(46.57, -105.83) * mm});
            skLineSegment(sketch, "E319.2.2.19", {"start": v(80.43, -97.37) * mm, "end": v(80.43, -105.83) * mm});
            skLineSegment(sketch, "E319.2.2.20", {"start": v(105.83, -71.97) * mm, "end": v(97.37, -71.97) * mm});
            skLineSegment(sketch, "E319.2.2.21", {"start": v(46.57, -97.37) * mm, "end": v(46.57, -105.83) * mm});
            skLineSegment(sketch, "E319.2.2.22", {"start": v(105.83, -46.57) * mm, "end": v(105.83, -55.03) * mm});
            skLineSegment(sketch, "E319.2.2.23", {"start": v(80.43, -46.57) * mm, "end": v(71.97, -46.57) * mm});
            skLineSegment(sketch, "E319.2.2.24", {"start": v(55.03, -46.57) * mm, "end": v(55.03, -55.03) * mm});
            skLineSegment(sketch, "E319.2.2.25", {"start": v(46.57, -71.97) * mm, "end": v(46.57, -80.43) * mm});
            skPoint(sketch, "E319.2.2.26", {"position": v(50.8, -76.2) * mm});
            skPoint(sketch, "E319.2.2.27", {"position": v(101.6, -50.8) * mm});
            skPoint(sketch, "E319.2.2.28", {"position": v(50.8, -50.8) * mm});
            skLineSegment(sketch, "E319.2.2.29", {"start": v(105.83, -97.37) * mm, "end": v(105.83, -105.83) * mm});
            skLineSegment(sketch, "E319.2.2.30", {"start": v(105.83, -71.97) * mm, "end": v(105.83, -80.43) * mm});
            skLineSegment(sketch, "E319.2.2.31", {"start": v(55.03, -97.37) * mm, "end": v(46.57, -97.37) * mm});
            skPoint(sketch, "E319.2.2.32", {"position": v(101.6, -101.6) * mm});
            skLineSegment(sketch, "E319.2.2.33", {"start": v(80.43, -97.37) * mm, "end": v(71.97, -97.37) * mm});
            skLineSegment(sketch, "E319.2.2.34", {"start": v(71.97, -46.57) * mm, "end": v(71.97, -55.03) * mm});
            skPoint(sketch, "E319.2.2.35", {"position": v(101.6, -50.8) * mm});
            skLineSegment(sketch, "E319.2.2.36", {"start": v(55.03, -71.97) * mm, "end": v(55.03, -80.43) * mm});
            skLineSegment(sketch, "E319.2.2.37", {"start": v(97.37, -97.37) * mm, "end": v(97.37, -105.83) * mm});
            skPoint(sketch, "E319.2.2.38", {"position": v(76.2, -50.8) * mm});
            skPoint(sketch, "E319.2.2.39", {"position": v(101.6, -76.2) * mm});
            skPoint(sketch, "E319.2.2.40", {"position": v(50.8, -101.6) * mm});
            skPoint(sketch, "E319.2.2.41", {"position": v(76.2, -101.6) * mm});
            skLineSegment(sketch, "E319.2.2.42", {"start": v(80.43, -105.83) * mm, "end": v(71.97, -105.83) * mm});
            skPoint(sketch, "E319.2.2.44", {"position": v(50.8, -50.8) * mm});
            skLineSegment(sketch, "E319.2.2.45", {"start": v(97.37, -46.57) * mm, "end": v(97.37, -55.03) * mm});
            skPoint(sketch, "E319.2.2.46", {"position": v(50.8, -76.2) * mm});
            skLineSegment(sketch, "E319.2.2.47", {"start": v(97.37, -71.97) * mm, "end": v(97.37, -80.43) * mm});
            skLineSegment(sketch, "E319.2.2.48", {"start": v(71.97, -97.37) * mm, "end": v(71.97, -105.83) * mm});
            skPoint(sketch, "E319.2.2.49", {"position": v(101.6, -101.6) * mm});
            skLineSegment(sketch, "E319.direction1", {"start": v(-105.83, 46.57) * mm, "end": v(-29.63, 46.57) * mm, "construction": true});
            skLineSegment(sketch, "E319.direction2", {"start": v(-105.83, 46.57) * mm, "end": v(-105.83, -29.63) * mm, "construction": true});
            skSolve(sketch);
        }
        {
            var Q0;
            Q0 = qSketchRegion(id + "F13", true);
            extrude(context, id + "F14", {"entities" : qUnion([Q0]), "operationType" : NewBodyOperationType.REMOVE, "oppositeDirection" : true, "depth" : 228.6 * mm, "offsetDistance" : 25.4 * mm});
        }
        {
            var Q0;
            Q0=makeQuery(id+"F1.opExtrude","SWEPT_FACE",FACE,{"disambiguationData":[OSD([sQuery(id+"F0.wireOp",EDGE,"E0.bottom")])]});
            var sketch = newSketch(context, id + "F15", { "sketchPlane" : qUnion([Q0])});
            skLineSegment(sketch, "E320.bottom", {"start": v(-63.5, 88.9) * mm, "end": v(-88.9, 88.9) * mm});
            skLineSegment(sketch, "E320.top", {"start": v(-63.5, 63.5) * mm, "end": v(-88.9, 63.5) * mm});
            skLineSegment(sketch, "E320.left", {"start": v(-63.5, 88.9) * mm, "end": v(-63.5, 63.5) * mm});
            skLineSegment(sketch, "E320.right", {"start": v(-88.9, 88.9) * mm, "end": v(-88.9, 63.5) * mm});
            skPoint(sketch, "E321", {"position": v(-101.6, 101.6) * mm});
            skLineSegment(sketch, "E322.bottom", {"start": v(-97.37, 105.83) * mm, "end": v(-105.83, 105.83) * mm});
            skLineSegment(sketch, "E322.top", {"start": v(-97.37, 97.37) * mm, "end": v(-105.83, 97.37) * mm});
            skLineSegment(sketch, "E322.left", {"start": v(-97.37, 105.83) * mm, "end": v(-97.37, 97.37) * mm});
            skLineSegment(sketch, "E322.right", {"start": v(-105.83, 105.83) * mm, "end": v(-105.83, 97.37) * mm});
            skPoint(sketch, "E323", {"position": v(-76.2, 101.6) * mm});
            skPoint(sketch, "E323.positionSnap0", {"position": v(-76.2, 88.9) * mm});
            skLineSegment(sketch, "E324.0.1.0", {"start": v(-97.37, 80.43) * mm, "end": v(-105.83, 80.43) * mm});
            skLineSegment(sketch, "E324.0.1.1", {"start": v(-97.37, 80.43) * mm, "end": v(-97.37, 71.97) * mm});
            skPoint(sketch, "E324.0.1.2", {"position": v(-101.6, 76.2) * mm});
            skLineSegment(sketch, "E324.0.1.3", {"start": v(-105.83, 80.43) * mm, "end": v(-105.83, 71.97) * mm});
            skLineSegment(sketch, "E324.0.1.4", {"start": v(-97.37, 71.97) * mm, "end": v(-105.83, 71.97) * mm});
            skPoint(sketch, "E324.0.1.5", {"position": v(-101.6, 76.2) * mm});
            skLineSegment(sketch, "E324.0.2.0", {"start": v(-97.37, 55.03) * mm, "end": v(-105.83, 55.03) * mm});
            skLineSegment(sketch, "E324.0.2.1", {"start": v(-97.37, 55.03) * mm, "end": v(-97.37, 46.57) * mm});
            skPoint(sketch, "E324.0.2.2", {"position": v(-101.6, 50.8) * mm});
            skLineSegment(sketch, "E324.0.2.3", {"start": v(-105.83, 55.03) * mm, "end": v(-105.83, 46.57) * mm});
            skLineSegment(sketch, "E324.0.2.4", {"start": v(-97.37, 46.57) * mm, "end": v(-105.83, 46.57) * mm});
            skPoint(sketch, "E324.0.2.5", {"position": v(-101.6, 50.8) * mm});
            skLineSegment(sketch, "E324.1.0.0", {"start": v(-71.97, 105.83) * mm, "end": v(-80.43, 105.83) * mm});
            skLineSegment(sketch, "E324.1.0.1", {"start": v(-71.97, 105.83) * mm, "end": v(-71.97, 97.37) * mm});
            skLineSegment(sketch, "E324.1.0.3", {"start": v(-80.43, 105.83) * mm, "end": v(-80.43, 97.37) * mm});
            skLineSegment(sketch, "E324.1.0.4", {"start": v(-71.97, 97.37) * mm, "end": v(-80.43, 97.37) * mm});
            skLineSegment(sketch, "E324.1.2.0", {"start": v(-71.97, 55.03) * mm, "end": v(-80.43, 55.03) * mm});
            skLineSegment(sketch, "E324.1.2.1", {"start": v(-71.97, 55.03) * mm, "end": v(-71.97, 46.57) * mm});
            skPoint(sketch, "E324.1.2.2", {"position": v(-76.2, 50.8) * mm});
            skLineSegment(sketch, "E324.1.2.3", {"start": v(-80.43, 55.03) * mm, "end": v(-80.43, 46.57) * mm});
            skLineSegment(sketch, "E324.1.2.4", {"start": v(-71.97, 46.57) * mm, "end": v(-80.43, 46.57) * mm});
            skPoint(sketch, "E324.1.2.5", {"position": v(-76.2, 50.8) * mm});
            skLineSegment(sketch, "E324.2.0.0", {"start": v(-46.57, 105.83) * mm, "end": v(-55.03, 105.83) * mm});
            skLineSegment(sketch, "E324.2.0.1", {"start": v(-46.57, 105.83) * mm, "end": v(-46.57, 97.37) * mm});
            skPoint(sketch, "E324.2.0.2", {"position": v(-50.8, 101.6) * mm});
            skLineSegment(sketch, "E324.2.0.3", {"start": v(-55.03, 105.83) * mm, "end": v(-55.03, 97.37) * mm});
            skLineSegment(sketch, "E324.2.0.4", {"start": v(-46.57, 97.37) * mm, "end": v(-55.03, 97.37) * mm});
            skPoint(sketch, "E324.2.0.5", {"position": v(-50.8, 101.6) * mm});
            skLineSegment(sketch, "E324.2.1.0", {"start": v(-46.57, 80.43) * mm, "end": v(-55.03, 80.43) * mm});
            skLineSegment(sketch, "E324.2.1.1", {"start": v(-46.57, 80.43) * mm, "end": v(-46.57, 71.97) * mm});
            skPoint(sketch, "E324.2.1.2", {"position": v(-50.8, 76.2) * mm});
            skLineSegment(sketch, "E324.2.1.3", {"start": v(-55.03, 80.43) * mm, "end": v(-55.03, 71.97) * mm});
            skLineSegment(sketch, "E324.2.1.4", {"start": v(-46.57, 71.97) * mm, "end": v(-55.03, 71.97) * mm});
            skPoint(sketch, "E324.2.1.5", {"position": v(-50.8, 76.2) * mm});
            skLineSegment(sketch, "E324.2.2.0", {"start": v(-46.57, 55.03) * mm, "end": v(-55.03, 55.03) * mm});
            skLineSegment(sketch, "E324.2.2.1", {"start": v(-46.57, 55.03) * mm, "end": v(-46.57, 46.57) * mm});
            skPoint(sketch, "E324.2.2.2", {"position": v(-50.8, 50.8) * mm});
            skLineSegment(sketch, "E324.2.2.3", {"start": v(-55.03, 55.03) * mm, "end": v(-55.03, 46.57) * mm});
            skLineSegment(sketch, "E324.2.2.4", {"start": v(-46.57, 46.57) * mm, "end": v(-55.03, 46.57) * mm});
            skPoint(sketch, "E324.2.2.5", {"position": v(-50.8, 50.8) * mm});
            skLineSegment(sketch, "E324.direction1", {"start": v(-105.83, 97.37) * mm, "end": v(-80.43, 97.37) * mm, "construction": true});
            skLineSegment(sketch, "E324.direction2", {"start": v(-105.83, 97.37) * mm, "end": v(-105.83, 71.97) * mm, "construction": true});
            skLineSegment(sketch, "E325.0.1.0", {"start": v(-105.83, -21.17) * mm, "end": v(-105.83, -29.63) * mm});
            skLineSegment(sketch, "E325.0.1.1", {"start": v(-46.57, 21.17) * mm, "end": v(-55.03, 21.17) * mm});
            skLineSegment(sketch, "E325.0.1.2", {"start": v(-46.57, -21.17) * mm, "end": v(-46.57, -29.63) * mm});
            skLineSegment(sketch, "E325.0.1.3", {"start": v(-105.83, 21.17) * mm, "end": v(-80.43, 21.17) * mm, "construction": true});
            skLineSegment(sketch, "E325.0.1.4", {"start": v(-71.97, 29.63) * mm, "end": v(-80.43, 29.63) * mm});
            skPoint(sketch, "E325.0.1.5", {"position": v(-101.6, -25.4) * mm});
            skLineSegment(sketch, "E325.0.1.6", {"start": v(-105.83, 21.17) * mm, "end": v(-105.83, -4.23) * mm, "construction": true});
            skPoint(sketch, "E325.0.1.7", {"position": v(-76.2, 12.7) * mm});
            skLineSegment(sketch, "E325.0.1.8", {"start": v(-97.37, 29.63) * mm, "end": v(-97.37, 21.17) * mm});
            skLineSegment(sketch, "E325.0.1.9", {"start": v(-97.37, 4.23) * mm, "end": v(-97.37, -4.23) * mm});
            skLineSegment(sketch, "E325.0.1.10", {"start": v(-97.37, -21.17) * mm, "end": v(-97.37, -29.63) * mm});
            skLineSegment(sketch, "E325.0.1.11", {"start": v(-55.03, 4.23) * mm, "end": v(-55.03, -4.23) * mm});
            skLineSegment(sketch, "E325.0.1.12", {"start": v(-80.43, -21.17) * mm, "end": v(-80.43, -29.63) * mm});
            skLineSegment(sketch, "E325.0.1.13", {"start": v(-55.03, 29.63) * mm, "end": v(-55.03, 21.17) * mm});
            skLineSegment(sketch, "E325.0.1.14", {"start": v(-97.37, -21.17) * mm, "end": v(-105.83, -21.17) * mm});
            skLineSegment(sketch, "E325.0.1.15", {"start": v(-80.43, 29.63) * mm, "end": v(-80.43, 21.17) * mm});
            skLineSegment(sketch, "E325.0.1.16", {"start": v(-97.37, 29.63) * mm, "end": v(-105.83, 29.63) * mm});
            skPoint(sketch, "E325.0.1.17", {"position": v(-50.8, 25.4) * mm});
            skLineSegment(sketch, "E325.0.1.18", {"start": v(-55.03, -21.17) * mm, "end": v(-55.03, -29.63) * mm});
            skLineSegment(sketch, "E325.0.1.19", {"start": v(-71.97, -21.17) * mm, "end": v(-71.97, -29.63) * mm});
            skPoint(sketch, "E325.0.1.20", {"position": v(-50.8, 0) * mm});
            skLineSegment(sketch, "E325.0.1.21", {"start": v(-46.57, 4.23) * mm, "end": v(-46.57, -4.23) * mm});
            skLineSegment(sketch, "E325.0.1.22", {"start": v(-63.5, 12.7) * mm, "end": v(-88.9, 12.7) * mm});
            skLineSegment(sketch, "E325.0.1.23", {"start": v(-46.57, 29.63) * mm, "end": v(-46.57, 21.17) * mm});
            skLineSegment(sketch, "E325.0.1.24", {"start": v(-46.57, -4.23) * mm, "end": v(-55.03, -4.23) * mm});
            skLineSegment(sketch, "E325.0.1.25", {"start": v(-71.97, -29.63) * mm, "end": v(-80.43, -29.63) * mm});
            skLineSegment(sketch, "E325.0.1.26", {"start": v(-97.37, -4.23) * mm, "end": v(-105.83, -4.23) * mm});
            skLineSegment(sketch, "E325.0.1.27", {"start": v(-97.37, 4.23) * mm, "end": v(-105.83, 4.23) * mm});
            skLineSegment(sketch, "E325.0.1.28", {"start": v(-71.97, 21.17) * mm, "end": v(-80.43, 21.17) * mm});
            skPoint(sketch, "E325.0.1.29", {"position": v(-50.8, -25.4) * mm});
            skLineSegment(sketch, "E325.0.1.30", {"start": v(-46.57, 29.63) * mm, "end": v(-55.03, 29.63) * mm});
            skLineSegment(sketch, "E325.0.1.31", {"start": v(-105.83, 29.63) * mm, "end": v(-105.83, 21.17) * mm});
            skLineSegment(sketch, "E325.0.1.32", {"start": v(-63.5, -12.7) * mm, "end": v(-88.9, -12.7) * mm});
            skLineSegment(sketch, "E325.0.1.33", {"start": v(-46.57, 4.23) * mm, "end": v(-55.03, 4.23) * mm});
            skPoint(sketch, "E325.0.1.34", {"position": v(-76.2, -25.4) * mm});
            skLineSegment(sketch, "E325.0.1.35", {"start": v(-46.57, -29.63) * mm, "end": v(-55.03, -29.63) * mm});
            skLineSegment(sketch, "E325.0.1.36", {"start": v(-97.37, -29.63) * mm, "end": v(-105.83, -29.63) * mm});
            skLineSegment(sketch, "E325.0.1.37", {"start": v(-63.5, 12.7) * mm, "end": v(-63.5, -12.7) * mm});
            skLineSegment(sketch, "E325.0.1.38", {"start": v(-71.97, 29.63) * mm, "end": v(-71.97, 21.17) * mm});
            skLineSegment(sketch, "E325.0.1.39", {"start": v(-46.57, -21.17) * mm, "end": v(-55.03, -21.17) * mm});
            skPoint(sketch, "E325.0.1.40", {"position": v(-101.6, 25.4) * mm});
            skLineSegment(sketch, "E325.0.1.41", {"start": v(-88.9, 12.7) * mm, "end": v(-88.9, -12.7) * mm});
            skPoint(sketch, "E325.0.1.42", {"position": v(-76.2, 25.4) * mm});
            skLineSegment(sketch, "E325.0.1.43", {"start": v(-71.97, -21.17) * mm, "end": v(-80.43, -21.17) * mm});
            skPoint(sketch, "E325.0.1.44", {"position": v(-101.6, 0) * mm});
            skLineSegment(sketch, "E325.0.1.45", {"start": v(-97.37, 21.17) * mm, "end": v(-105.83, 21.17) * mm});
            skPoint(sketch, "E325.0.1.46", {"position": v(-50.8, -25.4) * mm});
            skPoint(sketch, "E325.0.1.47", {"position": v(-50.8, 25.4) * mm});
            skPoint(sketch, "E325.0.1.48", {"position": v(-50.8, 0) * mm});
            skPoint(sketch, "E325.0.1.49", {"position": v(-76.2, 25.4) * mm});
            skPoint(sketch, "E325.0.1.50", {"position": v(-101.6, -25.4) * mm});
            skPoint(sketch, "E325.0.1.51", {"position": v(-101.6, 25.4) * mm});
            skPoint(sketch, "E325.0.1.52", {"position": v(-76.2, -25.4) * mm});
            skLineSegment(sketch, "E325.0.1.53", {"start": v(-105.83, 4.23) * mm, "end": v(-105.83, -4.23) * mm});
            skPoint(sketch, "E325.0.1.54", {"position": v(-101.6, 0) * mm});
            skPoint(sketch, "E325.0.1.55", {"position": v(-76.2, 25.4) * mm});
            skLineSegment(sketch, "E325.0.2.0", {"start": v(-105.83, -97.37) * mm, "end": v(-105.83, -105.83) * mm});
            skLineSegment(sketch, "E325.0.2.1", {"start": v(-46.57, -55.03) * mm, "end": v(-55.03, -55.03) * mm});
            skLineSegment(sketch, "E325.0.2.2", {"start": v(-46.57, -97.37) * mm, "end": v(-46.57, -105.83) * mm});
            skLineSegment(sketch, "E325.0.2.3", {"start": v(-105.83, -55.03) * mm, "end": v(-80.43, -55.03) * mm, "construction": true});
            skLineSegment(sketch, "E325.0.2.4", {"start": v(-71.97, -46.57) * mm, "end": v(-80.43, -46.57) * mm});
            skPoint(sketch, "E325.0.2.5", {"position": v(-101.6, -101.6) * mm});
            skLineSegment(sketch, "E325.0.2.6", {"start": v(-105.83, -55.03) * mm, "end": v(-105.83, -80.43) * mm, "construction": true});
            skPoint(sketch, "E325.0.2.7", {"position": v(-76.2, -63.5) * mm});
            skLineSegment(sketch, "E325.0.2.8", {"start": v(-97.37, -46.57) * mm, "end": v(-97.37, -55.03) * mm});
            skLineSegment(sketch, "E325.0.2.9", {"start": v(-97.37, -71.97) * mm, "end": v(-97.37, -80.43) * mm});
            skLineSegment(sketch, "E325.0.2.10", {"start": v(-97.37, -97.37) * mm, "end": v(-97.37, -105.83) * mm});
            skLineSegment(sketch, "E325.0.2.11", {"start": v(-55.03, -71.97) * mm, "end": v(-55.03, -80.43) * mm});
            skLineSegment(sketch, "E325.0.2.12", {"start": v(-80.43, -97.37) * mm, "end": v(-80.43, -105.83) * mm});
            skLineSegment(sketch, "E325.0.2.13", {"start": v(-55.03, -46.57) * mm, "end": v(-55.03, -55.03) * mm});
            skLineSegment(sketch, "E325.0.2.14", {"start": v(-97.37, -97.37) * mm, "end": v(-105.83, -97.37) * mm});
            skLineSegment(sketch, "E325.0.2.15", {"start": v(-80.43, -46.57) * mm, "end": v(-80.43, -55.03) * mm});
            skLineSegment(sketch, "E325.0.2.16", {"start": v(-97.37, -46.57) * mm, "end": v(-105.83, -46.57) * mm});
            skPoint(sketch, "E325.0.2.17", {"position": v(-50.8, -50.8) * mm});
            skLineSegment(sketch, "E325.0.2.18", {"start": v(-55.03, -97.37) * mm, "end": v(-55.03, -105.83) * mm});
            skLineSegment(sketch, "E325.0.2.19", {"start": v(-71.97, -97.37) * mm, "end": v(-71.97, -105.83) * mm});
            skPoint(sketch, "E325.0.2.20", {"position": v(-50.8, -76.2) * mm});
            skLineSegment(sketch, "E325.0.2.21", {"start": v(-46.57, -71.97) * mm, "end": v(-46.57, -80.43) * mm});
            skLineSegment(sketch, "E325.0.2.22", {"start": v(-63.5, -63.5) * mm, "end": v(-88.9, -63.5) * mm});
            skLineSegment(sketch, "E325.0.2.23", {"start": v(-46.57, -46.57) * mm, "end": v(-46.57, -55.03) * mm});
            skLineSegment(sketch, "E325.0.2.24", {"start": v(-46.57, -80.43) * mm, "end": v(-55.03, -80.43) * mm});
            skLineSegment(sketch, "E325.0.2.25", {"start": v(-71.97, -105.83) * mm, "end": v(-80.43, -105.83) * mm});
            skLineSegment(sketch, "E325.0.2.26", {"start": v(-97.37, -80.43) * mm, "end": v(-105.83, -80.43) * mm});
            skLineSegment(sketch, "E325.0.2.27", {"start": v(-97.37, -71.97) * mm, "end": v(-105.83, -71.97) * mm});
            skLineSegment(sketch, "E325.0.2.28", {"start": v(-71.97, -55.03) * mm, "end": v(-80.43, -55.03) * mm});
            skPoint(sketch, "E325.0.2.29", {"position": v(-50.8, -101.6) * mm});
            skLineSegment(sketch, "E325.0.2.30", {"start": v(-46.57, -46.57) * mm, "end": v(-55.03, -46.57) * mm});
            skLineSegment(sketch, "E325.0.2.31", {"start": v(-105.83, -46.57) * mm, "end": v(-105.83, -55.03) * mm});
            skLineSegment(sketch, "E325.0.2.32", {"start": v(-63.5, -88.9) * mm, "end": v(-88.9, -88.9) * mm});
            skLineSegment(sketch, "E325.0.2.33", {"start": v(-46.57, -71.97) * mm, "end": v(-55.03, -71.97) * mm});
            skPoint(sketch, "E325.0.2.34", {"position": v(-76.2, -101.6) * mm});
            skLineSegment(sketch, "E325.0.2.35", {"start": v(-46.57, -105.83) * mm, "end": v(-55.03, -105.83) * mm});
            skLineSegment(sketch, "E325.0.2.36", {"start": v(-97.37, -105.83) * mm, "end": v(-105.83, -105.83) * mm});
            skLineSegment(sketch, "E325.0.2.37", {"start": v(-63.5, -63.5) * mm, "end": v(-63.5, -88.9) * mm});
            skLineSegment(sketch, "E325.0.2.38", {"start": v(-71.97, -46.57) * mm, "end": v(-71.97, -55.03) * mm});
            skLineSegment(sketch, "E325.0.2.39", {"start": v(-46.57, -97.37) * mm, "end": v(-55.03, -97.37) * mm});
            skPoint(sketch, "E325.0.2.40", {"position": v(-101.6, -50.8) * mm});
            skLineSegment(sketch, "E325.0.2.41", {"start": v(-88.9, -63.5) * mm, "end": v(-88.9, -88.9) * mm});
            skPoint(sketch, "E325.0.2.42", {"position": v(-76.2, -50.8) * mm});
            skLineSegment(sketch, "E325.0.2.43", {"start": v(-71.97, -97.37) * mm, "end": v(-80.43, -97.37) * mm});
            skPoint(sketch, "E325.0.2.44", {"position": v(-101.6, -76.2) * mm});
            skLineSegment(sketch, "E325.0.2.45", {"start": v(-97.37, -55.03) * mm, "end": v(-105.83, -55.03) * mm});
            skPoint(sketch, "E325.0.2.46", {"position": v(-50.8, -101.6) * mm});
            skPoint(sketch, "E325.0.2.47", {"position": v(-50.8, -50.8) * mm});
            skPoint(sketch, "E325.0.2.48", {"position": v(-50.8, -76.2) * mm});
            skPoint(sketch, "E325.0.2.49", {"position": v(-76.2, -50.8) * mm});
            skPoint(sketch, "E325.0.2.50", {"position": v(-101.6, -101.6) * mm});
            skPoint(sketch, "E325.0.2.51", {"position": v(-101.6, -50.8) * mm});
            skPoint(sketch, "E325.0.2.52", {"position": v(-76.2, -101.6) * mm});
            skLineSegment(sketch, "E325.0.2.53", {"start": v(-105.83, -71.97) * mm, "end": v(-105.83, -80.43) * mm});
            skPoint(sketch, "E325.0.2.54", {"position": v(-101.6, -76.2) * mm});
            skPoint(sketch, "E325.0.2.55", {"position": v(-76.2, -50.8) * mm});
            skLineSegment(sketch, "E325.1.0.0", {"start": v(-29.63, 55.03) * mm, "end": v(-29.63, 46.57) * mm});
            skLineSegment(sketch, "E325.1.0.1", {"start": v(29.63, 97.37) * mm, "end": v(21.17, 97.37) * mm});
            skLineSegment(sketch, "E325.1.0.2", {"start": v(29.63, 55.03) * mm, "end": v(29.63, 46.57) * mm});
            skLineSegment(sketch, "E325.1.0.3", {"start": v(-29.63, 97.37) * mm, "end": v(-4.23, 97.37) * mm, "construction": true});
            skLineSegment(sketch, "E325.1.0.4", {"start": v(4.23, 105.83) * mm, "end": v(-4.23, 105.83) * mm});
            skPoint(sketch, "E325.1.0.5", {"position": v(-25.4, 50.8) * mm});
            skLineSegment(sketch, "E325.1.0.6", {"start": v(-29.63, 97.37) * mm, "end": v(-29.63, 71.97) * mm, "construction": true});
            skPoint(sketch, "E325.1.0.7", {"position": v(0, 88.9) * mm});
            skLineSegment(sketch, "E325.1.0.8", {"start": v(-21.17, 105.83) * mm, "end": v(-21.17, 97.37) * mm});
            skLineSegment(sketch, "E325.1.0.9", {"start": v(-21.17, 80.43) * mm, "end": v(-21.17, 71.97) * mm});
            skLineSegment(sketch, "E325.1.0.10", {"start": v(-21.17, 55.03) * mm, "end": v(-21.17, 46.57) * mm});
            skLineSegment(sketch, "E325.1.0.11", {"start": v(21.17, 80.43) * mm, "end": v(21.17, 71.97) * mm});
            skLineSegment(sketch, "E325.1.0.12", {"start": v(-4.23, 55.03) * mm, "end": v(-4.23, 46.57) * mm});
            skLineSegment(sketch, "E325.1.0.13", {"start": v(21.17, 105.83) * mm, "end": v(21.17, 97.37) * mm});
            skLineSegment(sketch, "E325.1.0.14", {"start": v(-21.17, 55.03) * mm, "end": v(-29.63, 55.03) * mm});
            skLineSegment(sketch, "E325.1.0.15", {"start": v(-4.23, 105.83) * mm, "end": v(-4.23, 97.37) * mm});
            skLineSegment(sketch, "E325.1.0.16", {"start": v(-21.17, 105.83) * mm, "end": v(-29.63, 105.83) * mm});
            skPoint(sketch, "E325.1.0.17", {"position": v(25.4, 101.6) * mm});
            skLineSegment(sketch, "E325.1.0.18", {"start": v(21.17, 55.03) * mm, "end": v(21.17, 46.57) * mm});
            skLineSegment(sketch, "E325.1.0.19", {"start": v(4.23, 55.03) * mm, "end": v(4.23, 46.57) * mm});
            skPoint(sketch, "E325.1.0.20", {"position": v(25.4, 76.2) * mm});
            skLineSegment(sketch, "E325.1.0.21", {"start": v(29.63, 80.43) * mm, "end": v(29.63, 71.97) * mm});
            skLineSegment(sketch, "E325.1.0.22", {"start": v(12.7, 88.9) * mm, "end": v(-12.7, 88.9) * mm});
            skLineSegment(sketch, "E325.1.0.23", {"start": v(29.63, 105.83) * mm, "end": v(29.63, 97.37) * mm});
            skLineSegment(sketch, "E325.1.0.24", {"start": v(29.63, 71.97) * mm, "end": v(21.17, 71.97) * mm});
            skLineSegment(sketch, "E325.1.0.25", {"start": v(4.23, 46.57) * mm, "end": v(-4.23, 46.57) * mm});
            skLineSegment(sketch, "E325.1.0.26", {"start": v(-21.17, 71.97) * mm, "end": v(-29.63, 71.97) * mm});
            skLineSegment(sketch, "E325.1.0.27", {"start": v(-21.17, 80.43) * mm, "end": v(-29.63, 80.43) * mm});
            skLineSegment(sketch, "E325.1.0.28", {"start": v(4.23, 97.37) * mm, "end": v(-4.23, 97.37) * mm});
            skPoint(sketch, "E325.1.0.29", {"position": v(25.4, 50.8) * mm});
            skLineSegment(sketch, "E325.1.0.30", {"start": v(29.63, 105.83) * mm, "end": v(21.17, 105.83) * mm});
            skLineSegment(sketch, "E325.1.0.31", {"start": v(-29.63, 105.83) * mm, "end": v(-29.63, 97.37) * mm});
            skLineSegment(sketch, "E325.1.0.32", {"start": v(12.7, 63.5) * mm, "end": v(-12.7, 63.5) * mm});
            skLineSegment(sketch, "E325.1.0.33", {"start": v(29.63, 80.43) * mm, "end": v(21.17, 80.43) * mm});
            skPoint(sketch, "E325.1.0.34", {"position": v(0, 50.8) * mm});
            skLineSegment(sketch, "E325.1.0.35", {"start": v(29.63, 46.57) * mm, "end": v(21.17, 46.57) * mm});
            skLineSegment(sketch, "E325.1.0.36", {"start": v(-21.17, 46.57) * mm, "end": v(-29.63, 46.57) * mm});
            skLineSegment(sketch, "E325.1.0.37", {"start": v(12.7, 88.9) * mm, "end": v(12.7, 63.5) * mm});
            skLineSegment(sketch, "E325.1.0.38", {"start": v(4.23, 105.83) * mm, "end": v(4.23, 97.37) * mm});
            skLineSegment(sketch, "E325.1.0.39", {"start": v(29.63, 55.03) * mm, "end": v(21.17, 55.03) * mm});
            skPoint(sketch, "E325.1.0.40", {"position": v(-25.4, 101.6) * mm});
            skLineSegment(sketch, "E325.1.0.41", {"start": v(-12.7, 88.9) * mm, "end": v(-12.7, 63.5) * mm});
            skPoint(sketch, "E325.1.0.42", {"position": v(0, 101.6) * mm});
            skLineSegment(sketch, "E325.1.0.43", {"start": v(4.23, 55.03) * mm, "end": v(-4.23, 55.03) * mm});
            skPoint(sketch, "E325.1.0.44", {"position": v(-25.4, 76.2) * mm});
            skLineSegment(sketch, "E325.1.0.45", {"start": v(-21.17, 97.37) * mm, "end": v(-29.63, 97.37) * mm});
            skPoint(sketch, "E325.1.0.46", {"position": v(25.4, 50.8) * mm});
            skPoint(sketch, "E325.1.0.47", {"position": v(25.4, 101.6) * mm});
            skPoint(sketch, "E325.1.0.48", {"position": v(25.4, 76.2) * mm});
            skPoint(sketch, "E325.1.0.49", {"position": v(0, 101.6) * mm});
            skPoint(sketch, "E325.1.0.50", {"position": v(-25.4, 50.8) * mm});
            skPoint(sketch, "E325.1.0.51", {"position": v(-25.4, 101.6) * mm});
            skPoint(sketch, "E325.1.0.52", {"position": v(0, 50.8) * mm});
            skLineSegment(sketch, "E325.1.0.53", {"start": v(-29.63, 80.43) * mm, "end": v(-29.63, 71.97) * mm});
            skPoint(sketch, "E325.1.0.54", {"position": v(-25.4, 76.2) * mm});
            skPoint(sketch, "E325.1.0.55", {"position": v(0, 101.6) * mm});
            skLineSegment(sketch, "E325.1.2.0", {"start": v(-29.63, -97.37) * mm, "end": v(-29.63, -105.83) * mm});
            skLineSegment(sketch, "E325.1.2.1", {"start": v(29.63, -55.03) * mm, "end": v(21.17, -55.03) * mm});
            skLineSegment(sketch, "E325.1.2.2", {"start": v(29.63, -97.37) * mm, "end": v(29.63, -105.83) * mm});
            skLineSegment(sketch, "E325.1.2.3", {"start": v(-29.63, -55.03) * mm, "end": v(-4.23, -55.03) * mm, "construction": true});
            skLineSegment(sketch, "E325.1.2.4", {"start": v(4.23, -46.57) * mm, "end": v(-4.23, -46.57) * mm});
            skPoint(sketch, "E325.1.2.5", {"position": v(-25.4, -101.6) * mm});
            skLineSegment(sketch, "E325.1.2.6", {"start": v(-29.63, -55.03) * mm, "end": v(-29.63, -80.43) * mm, "construction": true});
            skPoint(sketch, "E325.1.2.7", {"position": v(0, -63.5) * mm});
            skLineSegment(sketch, "E325.1.2.8", {"start": v(-21.17, -46.57) * mm, "end": v(-21.17, -55.03) * mm});
            skLineSegment(sketch, "E325.1.2.9", {"start": v(-21.17, -71.97) * mm, "end": v(-21.17, -80.43) * mm});
            skLineSegment(sketch, "E325.1.2.10", {"start": v(-21.17, -97.37) * mm, "end": v(-21.17, -105.83) * mm});
            skLineSegment(sketch, "E325.1.2.11", {"start": v(21.17, -71.97) * mm, "end": v(21.17, -80.43) * mm});
            skLineSegment(sketch, "E325.1.2.12", {"start": v(-4.23, -97.37) * mm, "end": v(-4.23, -105.83) * mm});
            skLineSegment(sketch, "E325.1.2.13", {"start": v(21.17, -46.57) * mm, "end": v(21.17, -55.03) * mm});
            skLineSegment(sketch, "E325.1.2.14", {"start": v(-21.17, -97.37) * mm, "end": v(-29.63, -97.37) * mm});
            skLineSegment(sketch, "E325.1.2.15", {"start": v(-4.23, -46.57) * mm, "end": v(-4.23, -55.03) * mm});
            skLineSegment(sketch, "E325.1.2.16", {"start": v(-21.17, -46.57) * mm, "end": v(-29.63, -46.57) * mm});
            skPoint(sketch, "E325.1.2.17", {"position": v(25.4, -50.8) * mm});
            skLineSegment(sketch, "E325.1.2.18", {"start": v(21.17, -97.37) * mm, "end": v(21.17, -105.83) * mm});
            skLineSegment(sketch, "E325.1.2.19", {"start": v(4.23, -97.37) * mm, "end": v(4.23, -105.83) * mm});
            skPoint(sketch, "E325.1.2.20", {"position": v(25.4, -76.2) * mm});
            skLineSegment(sketch, "E325.1.2.21", {"start": v(29.63, -71.97) * mm, "end": v(29.63, -80.43) * mm});
            skLineSegment(sketch, "E325.1.2.22", {"start": v(12.7, -63.5) * mm, "end": v(-12.7, -63.5) * mm});
            skLineSegment(sketch, "E325.1.2.23", {"start": v(29.63, -46.57) * mm, "end": v(29.63, -55.03) * mm});
            skLineSegment(sketch, "E325.1.2.24", {"start": v(29.63, -80.43) * mm, "end": v(21.17, -80.43) * mm});
            skLineSegment(sketch, "E325.1.2.25", {"start": v(4.23, -105.83) * mm, "end": v(-4.23, -105.83) * mm});
            skLineSegment(sketch, "E325.1.2.26", {"start": v(-21.17, -80.43) * mm, "end": v(-29.63, -80.43) * mm});
            skLineSegment(sketch, "E325.1.2.27", {"start": v(-21.17, -71.97) * mm, "end": v(-29.63, -71.97) * mm});
            skLineSegment(sketch, "E325.1.2.28", {"start": v(4.23, -55.03) * mm, "end": v(-4.23, -55.03) * mm});
            skPoint(sketch, "E325.1.2.29", {"position": v(25.4, -101.6) * mm});
            skLineSegment(sketch, "E325.1.2.30", {"start": v(29.63, -46.57) * mm, "end": v(21.17, -46.57) * mm});
            skLineSegment(sketch, "E325.1.2.31", {"start": v(-29.63, -46.57) * mm, "end": v(-29.63, -55.03) * mm});
            skLineSegment(sketch, "E325.1.2.32", {"start": v(12.7, -88.9) * mm, "end": v(-12.7, -88.9) * mm});
            skLineSegment(sketch, "E325.1.2.33", {"start": v(29.63, -71.97) * mm, "end": v(21.17, -71.97) * mm});
            skPoint(sketch, "E325.1.2.34", {"position": v(0, -101.6) * mm});
            skLineSegment(sketch, "E325.1.2.35", {"start": v(29.63, -105.83) * mm, "end": v(21.17, -105.83) * mm});
            skLineSegment(sketch, "E325.1.2.36", {"start": v(-21.17, -105.83) * mm, "end": v(-29.63, -105.83) * mm});
            skLineSegment(sketch, "E325.1.2.37", {"start": v(12.7, -63.5) * mm, "end": v(12.7, -88.9) * mm});
            skLineSegment(sketch, "E325.1.2.38", {"start": v(4.23, -46.57) * mm, "end": v(4.23, -55.03) * mm});
            skLineSegment(sketch, "E325.1.2.39", {"start": v(29.63, -97.37) * mm, "end": v(21.17, -97.37) * mm});
            skPoint(sketch, "E325.1.2.40", {"position": v(-25.4, -50.8) * mm});
            skLineSegment(sketch, "E325.1.2.41", {"start": v(-12.7, -63.5) * mm, "end": v(-12.7, -88.9) * mm});
            skPoint(sketch, "E325.1.2.42", {"position": v(0, -50.8) * mm});
            skLineSegment(sketch, "E325.1.2.43", {"start": v(4.23, -97.37) * mm, "end": v(-4.23, -97.37) * mm});
            skPoint(sketch, "E325.1.2.44", {"position": v(-25.4, -76.2) * mm});
            skLineSegment(sketch, "E325.1.2.45", {"start": v(-21.17, -55.03) * mm, "end": v(-29.63, -55.03) * mm});
            skPoint(sketch, "E325.1.2.46", {"position": v(25.4, -101.6) * mm});
            skPoint(sketch, "E325.1.2.47", {"position": v(25.4, -50.8) * mm});
            skPoint(sketch, "E325.1.2.48", {"position": v(25.4, -76.2) * mm});
            skPoint(sketch, "E325.1.2.49", {"position": v(0, -50.8) * mm});
            skPoint(sketch, "E325.1.2.50", {"position": v(-25.4, -101.6) * mm});
            skPoint(sketch, "E325.1.2.51", {"position": v(-25.4, -50.8) * mm});
            skPoint(sketch, "E325.1.2.52", {"position": v(0, -101.6) * mm});
            skLineSegment(sketch, "E325.1.2.53", {"start": v(-29.63, -71.97) * mm, "end": v(-29.63, -80.43) * mm});
            skPoint(sketch, "E325.1.2.54", {"position": v(-25.4, -76.2) * mm});
            skPoint(sketch, "E325.1.2.55", {"position": v(0, -50.8) * mm});
            skLineSegment(sketch, "E325.2.0.0", {"start": v(46.57, 55.03) * mm, "end": v(46.57, 46.57) * mm});
            skLineSegment(sketch, "E325.2.0.1", {"start": v(105.83, 97.37) * mm, "end": v(97.37, 97.37) * mm});
            skLineSegment(sketch, "E325.2.0.2", {"start": v(105.83, 55.03) * mm, "end": v(105.83, 46.57) * mm});
            skLineSegment(sketch, "E325.2.0.3", {"start": v(46.57, 97.37) * mm, "end": v(71.97, 97.37) * mm, "construction": true});
            skLineSegment(sketch, "E325.2.0.4", {"start": v(80.43, 105.83) * mm, "end": v(71.97, 105.83) * mm});
            skPoint(sketch, "E325.2.0.5", {"position": v(50.8, 50.8) * mm});
            skLineSegment(sketch, "E325.2.0.6", {"start": v(46.57, 97.37) * mm, "end": v(46.57, 71.97) * mm, "construction": true});
            skPoint(sketch, "E325.2.0.7", {"position": v(76.2, 88.9) * mm});
            skLineSegment(sketch, "E325.2.0.8", {"start": v(55.03, 105.83) * mm, "end": v(55.03, 97.37) * mm});
            skLineSegment(sketch, "E325.2.0.9", {"start": v(55.03, 80.43) * mm, "end": v(55.03, 71.97) * mm});
            skLineSegment(sketch, "E325.2.0.10", {"start": v(55.03, 55.03) * mm, "end": v(55.03, 46.57) * mm});
            skLineSegment(sketch, "E325.2.0.11", {"start": v(97.37, 80.43) * mm, "end": v(97.37, 71.97) * mm});
            skLineSegment(sketch, "E325.2.0.12", {"start": v(71.97, 55.03) * mm, "end": v(71.97, 46.57) * mm});
            skLineSegment(sketch, "E325.2.0.13", {"start": v(97.37, 105.83) * mm, "end": v(97.37, 97.37) * mm});
            skLineSegment(sketch, "E325.2.0.14", {"start": v(55.03, 55.03) * mm, "end": v(46.57, 55.03) * mm});
            skLineSegment(sketch, "E325.2.0.15", {"start": v(71.97, 105.83) * mm, "end": v(71.97, 97.37) * mm});
            skLineSegment(sketch, "E325.2.0.16", {"start": v(55.03, 105.83) * mm, "end": v(46.57, 105.83) * mm});
            skPoint(sketch, "E325.2.0.17", {"position": v(101.6, 101.6) * mm});
            skLineSegment(sketch, "E325.2.0.18", {"start": v(97.37, 55.03) * mm, "end": v(97.37, 46.57) * mm});
            skLineSegment(sketch, "E325.2.0.19", {"start": v(80.43, 55.03) * mm, "end": v(80.43, 46.57) * mm});
            skPoint(sketch, "E325.2.0.20", {"position": v(101.6, 76.2) * mm});
            skLineSegment(sketch, "E325.2.0.21", {"start": v(105.83, 80.43) * mm, "end": v(105.83, 71.97) * mm});
            skLineSegment(sketch, "E325.2.0.22", {"start": v(88.9, 88.9) * mm, "end": v(63.5, 88.9) * mm});
            skLineSegment(sketch, "E325.2.0.23", {"start": v(105.83, 105.83) * mm, "end": v(105.83, 97.37) * mm});
            skLineSegment(sketch, "E325.2.0.24", {"start": v(105.83, 71.97) * mm, "end": v(97.37, 71.97) * mm});
            skLineSegment(sketch, "E325.2.0.25", {"start": v(80.43, 46.57) * mm, "end": v(71.97, 46.57) * mm});
            skLineSegment(sketch, "E325.2.0.26", {"start": v(55.03, 71.97) * mm, "end": v(46.57, 71.97) * mm});
            skLineSegment(sketch, "E325.2.0.27", {"start": v(55.03, 80.43) * mm, "end": v(46.57, 80.43) * mm});
            skLineSegment(sketch, "E325.2.0.28", {"start": v(80.43, 97.37) * mm, "end": v(71.97, 97.37) * mm});
            skPoint(sketch, "E325.2.0.29", {"position": v(101.6, 50.8) * mm});
            skLineSegment(sketch, "E325.2.0.30", {"start": v(105.83, 105.83) * mm, "end": v(97.37, 105.83) * mm});
            skLineSegment(sketch, "E325.2.0.31", {"start": v(46.57, 105.83) * mm, "end": v(46.57, 97.37) * mm});
            skLineSegment(sketch, "E325.2.0.32", {"start": v(88.9, 63.5) * mm, "end": v(63.5, 63.5) * mm});
            skLineSegment(sketch, "E325.2.0.33", {"start": v(105.83, 80.43) * mm, "end": v(97.37, 80.43) * mm});
            skPoint(sketch, "E325.2.0.34", {"position": v(76.2, 50.8) * mm});
            skLineSegment(sketch, "E325.2.0.35", {"start": v(105.83, 46.57) * mm, "end": v(97.37, 46.57) * mm});
            skLineSegment(sketch, "E325.2.0.36", {"start": v(55.03, 46.57) * mm, "end": v(46.57, 46.57) * mm});
            skLineSegment(sketch, "E325.2.0.37", {"start": v(88.9, 88.9) * mm, "end": v(88.9, 63.5) * mm});
            skLineSegment(sketch, "E325.2.0.38", {"start": v(80.43, 105.83) * mm, "end": v(80.43, 97.37) * mm});
            skLineSegment(sketch, "E325.2.0.39", {"start": v(105.83, 55.03) * mm, "end": v(97.37, 55.03) * mm});
            skPoint(sketch, "E325.2.0.40", {"position": v(50.8, 101.6) * mm});
            skLineSegment(sketch, "E325.2.0.41", {"start": v(63.5, 88.9) * mm, "end": v(63.5, 63.5) * mm});
            skPoint(sketch, "E325.2.0.42", {"position": v(76.2, 101.6) * mm});
            skLineSegment(sketch, "E325.2.0.43", {"start": v(80.43, 55.03) * mm, "end": v(71.97, 55.03) * mm});
            skPoint(sketch, "E325.2.0.44", {"position": v(50.8, 76.2) * mm});
            skLineSegment(sketch, "E325.2.0.45", {"start": v(55.03, 97.37) * mm, "end": v(46.57, 97.37) * mm});
            skPoint(sketch, "E325.2.0.46", {"position": v(101.6, 50.8) * mm});
            skPoint(sketch, "E325.2.0.47", {"position": v(101.6, 101.6) * mm});
            skPoint(sketch, "E325.2.0.48", {"position": v(101.6, 76.2) * mm});
            skPoint(sketch, "E325.2.0.49", {"position": v(76.2, 101.6) * mm});
            skPoint(sketch, "E325.2.0.50", {"position": v(50.8, 50.8) * mm});
            skPoint(sketch, "E325.2.0.51", {"position": v(50.8, 101.6) * mm});
            skPoint(sketch, "E325.2.0.52", {"position": v(76.2, 50.8) * mm});
            skLineSegment(sketch, "E325.2.0.53", {"start": v(46.57, 80.43) * mm, "end": v(46.57, 71.97) * mm});
            skPoint(sketch, "E325.2.0.54", {"position": v(50.8, 76.2) * mm});
            skPoint(sketch, "E325.2.0.55", {"position": v(76.2, 101.6) * mm});
            skLineSegment(sketch, "E325.2.1.0", {"start": v(46.57, -21.17) * mm, "end": v(46.57, -29.63) * mm});
            skLineSegment(sketch, "E325.2.1.1", {"start": v(105.83, 21.17) * mm, "end": v(97.37, 21.17) * mm});
            skLineSegment(sketch, "E325.2.1.2", {"start": v(105.83, -21.17) * mm, "end": v(105.83, -29.63) * mm});
            skLineSegment(sketch, "E325.2.1.3", {"start": v(46.57, 21.17) * mm, "end": v(71.97, 21.17) * mm, "construction": true});
            skLineSegment(sketch, "E325.2.1.4", {"start": v(80.43, 29.63) * mm, "end": v(71.97, 29.63) * mm});
            skPoint(sketch, "E325.2.1.5", {"position": v(50.8, -25.4) * mm});
            skLineSegment(sketch, "E325.2.1.6", {"start": v(46.57, 21.17) * mm, "end": v(46.57, -4.23) * mm, "construction": true});
            skPoint(sketch, "E325.2.1.7", {"position": v(76.2, 12.7) * mm});
            skLineSegment(sketch, "E325.2.1.8", {"start": v(55.03, 29.63) * mm, "end": v(55.03, 21.17) * mm});
            skLineSegment(sketch, "E325.2.1.9", {"start": v(55.03, 4.23) * mm, "end": v(55.03, -4.23) * mm});
            skLineSegment(sketch, "E325.2.1.10", {"start": v(55.03, -21.17) * mm, "end": v(55.03, -29.63) * mm});
            skLineSegment(sketch, "E325.2.1.11", {"start": v(97.37, 4.23) * mm, "end": v(97.37, -4.23) * mm});
            skLineSegment(sketch, "E325.2.1.12", {"start": v(71.97, -21.17) * mm, "end": v(71.97, -29.63) * mm});
            skLineSegment(sketch, "E325.2.1.13", {"start": v(97.37, 29.63) * mm, "end": v(97.37, 21.17) * mm});
            skLineSegment(sketch, "E325.2.1.14", {"start": v(55.03, -21.17) * mm, "end": v(46.57, -21.17) * mm});
            skLineSegment(sketch, "E325.2.1.15", {"start": v(71.97, 29.63) * mm, "end": v(71.97, 21.17) * mm});
            skLineSegment(sketch, "E325.2.1.16", {"start": v(55.03, 29.63) * mm, "end": v(46.57, 29.63) * mm});
            skPoint(sketch, "E325.2.1.17", {"position": v(101.6, 25.4) * mm});
            skLineSegment(sketch, "E325.2.1.18", {"start": v(97.37, -21.17) * mm, "end": v(97.37, -29.63) * mm});
            skLineSegment(sketch, "E325.2.1.19", {"start": v(80.43, -21.17) * mm, "end": v(80.43, -29.63) * mm});
            skPoint(sketch, "E325.2.1.20", {"position": v(101.6, 0) * mm});
            skLineSegment(sketch, "E325.2.1.21", {"start": v(105.83, 4.23) * mm, "end": v(105.83, -4.23) * mm});
            skLineSegment(sketch, "E325.2.1.22", {"start": v(88.9, 12.7) * mm, "end": v(63.5, 12.7) * mm});
            skLineSegment(sketch, "E325.2.1.23", {"start": v(105.83, 29.63) * mm, "end": v(105.83, 21.17) * mm});
            skLineSegment(sketch, "E325.2.1.24", {"start": v(105.83, -4.23) * mm, "end": v(97.37, -4.23) * mm});
            skLineSegment(sketch, "E325.2.1.25", {"start": v(80.43, -29.63) * mm, "end": v(71.97, -29.63) * mm});
            skLineSegment(sketch, "E325.2.1.26", {"start": v(55.03, -4.23) * mm, "end": v(46.57, -4.23) * mm});
            skLineSegment(sketch, "E325.2.1.27", {"start": v(55.03, 4.23) * mm, "end": v(46.57, 4.23) * mm});
            skLineSegment(sketch, "E325.2.1.28", {"start": v(80.43, 21.17) * mm, "end": v(71.97, 21.17) * mm});
            skPoint(sketch, "E325.2.1.29", {"position": v(101.6, -25.4) * mm});
            skLineSegment(sketch, "E325.2.1.30", {"start": v(105.83, 29.63) * mm, "end": v(97.37, 29.63) * mm});
            skLineSegment(sketch, "E325.2.1.31", {"start": v(46.57, 29.63) * mm, "end": v(46.57, 21.17) * mm});
            skLineSegment(sketch, "E325.2.1.32", {"start": v(88.9, -12.7) * mm, "end": v(63.5, -12.7) * mm});
            skLineSegment(sketch, "E325.2.1.33", {"start": v(105.83, 4.23) * mm, "end": v(97.37, 4.23) * mm});
            skPoint(sketch, "E325.2.1.34", {"position": v(76.2, -25.4) * mm});
            skLineSegment(sketch, "E325.2.1.35", {"start": v(105.83, -29.63) * mm, "end": v(97.37, -29.63) * mm});
            skLineSegment(sketch, "E325.2.1.36", {"start": v(55.03, -29.63) * mm, "end": v(46.57, -29.63) * mm});
            skLineSegment(sketch, "E325.2.1.37", {"start": v(88.9, 12.7) * mm, "end": v(88.9, -12.7) * mm});
            skLineSegment(sketch, "E325.2.1.38", {"start": v(80.43, 29.63) * mm, "end": v(80.43, 21.17) * mm});
            skLineSegment(sketch, "E325.2.1.39", {"start": v(105.83, -21.17) * mm, "end": v(97.37, -21.17) * mm});
            skPoint(sketch, "E325.2.1.40", {"position": v(50.8, 25.4) * mm});
            skLineSegment(sketch, "E325.2.1.41", {"start": v(63.5, 12.7) * mm, "end": v(63.5, -12.7) * mm});
            skPoint(sketch, "E325.2.1.42", {"position": v(76.2, 25.4) * mm});
            skLineSegment(sketch, "E325.2.1.43", {"start": v(80.43, -21.17) * mm, "end": v(71.97, -21.17) * mm});
            skPoint(sketch, "E325.2.1.44", {"position": v(50.8, 0) * mm});
            skLineSegment(sketch, "E325.2.1.45", {"start": v(55.03, 21.17) * mm, "end": v(46.57, 21.17) * mm});
            skPoint(sketch, "E325.2.1.46", {"position": v(101.6, -25.4) * mm});
            skPoint(sketch, "E325.2.1.47", {"position": v(101.6, 25.4) * mm});
            skPoint(sketch, "E325.2.1.48", {"position": v(101.6, 0) * mm});
            skPoint(sketch, "E325.2.1.49", {"position": v(76.2, 25.4) * mm});
            skPoint(sketch, "E325.2.1.50", {"position": v(50.8, -25.4) * mm});
            skPoint(sketch, "E325.2.1.51", {"position": v(50.8, 25.4) * mm});
            skPoint(sketch, "E325.2.1.52", {"position": v(76.2, -25.4) * mm});
            skLineSegment(sketch, "E325.2.1.53", {"start": v(46.57, 4.23) * mm, "end": v(46.57, -4.23) * mm});
            skPoint(sketch, "E325.2.1.54", {"position": v(50.8, 0) * mm});
            skPoint(sketch, "E325.2.1.55", {"position": v(76.2, 25.4) * mm});
            skLineSegment(sketch, "E325.2.2.0", {"start": v(46.57, -97.37) * mm, "end": v(46.57, -105.83) * mm});
            skLineSegment(sketch, "E325.2.2.1", {"start": v(105.83, -55.03) * mm, "end": v(97.37, -55.03) * mm});
            skLineSegment(sketch, "E325.2.2.2", {"start": v(105.83, -97.37) * mm, "end": v(105.83, -105.83) * mm});
            skLineSegment(sketch, "E325.2.2.3", {"start": v(46.57, -55.03) * mm, "end": v(71.97, -55.03) * mm, "construction": true});
            skLineSegment(sketch, "E325.2.2.4", {"start": v(80.43, -46.57) * mm, "end": v(71.97, -46.57) * mm});
            skPoint(sketch, "E325.2.2.5", {"position": v(50.8, -101.6) * mm});
            skLineSegment(sketch, "E325.2.2.6", {"start": v(46.57, -55.03) * mm, "end": v(46.57, -80.43) * mm, "construction": true});
            skPoint(sketch, "E325.2.2.7", {"position": v(76.2, -63.5) * mm});
            skLineSegment(sketch, "E325.2.2.8", {"start": v(55.03, -46.57) * mm, "end": v(55.03, -55.03) * mm});
            skLineSegment(sketch, "E325.2.2.9", {"start": v(55.03, -71.97) * mm, "end": v(55.03, -80.43) * mm});
            skLineSegment(sketch, "E325.2.2.10", {"start": v(55.03, -97.37) * mm, "end": v(55.03, -105.83) * mm});
            skLineSegment(sketch, "E325.2.2.11", {"start": v(97.37, -71.97) * mm, "end": v(97.37, -80.43) * mm});
            skLineSegment(sketch, "E325.2.2.12", {"start": v(71.97, -97.37) * mm, "end": v(71.97, -105.83) * mm});
            skLineSegment(sketch, "E325.2.2.13", {"start": v(97.37, -46.57) * mm, "end": v(97.37, -55.03) * mm});
            skLineSegment(sketch, "E325.2.2.14", {"start": v(55.03, -97.37) * mm, "end": v(46.57, -97.37) * mm});
            skLineSegment(sketch, "E325.2.2.15", {"start": v(71.97, -46.57) * mm, "end": v(71.97, -55.03) * mm});
            skLineSegment(sketch, "E325.2.2.16", {"start": v(55.03, -46.57) * mm, "end": v(46.57, -46.57) * mm});
            skPoint(sketch, "E325.2.2.17", {"position": v(101.6, -50.8) * mm});
            skLineSegment(sketch, "E325.2.2.18", {"start": v(97.37, -97.37) * mm, "end": v(97.37, -105.83) * mm});
            skLineSegment(sketch, "E325.2.2.19", {"start": v(80.43, -97.37) * mm, "end": v(80.43, -105.83) * mm});
            skPoint(sketch, "E325.2.2.20", {"position": v(101.6, -76.2) * mm});
            skLineSegment(sketch, "E325.2.2.21", {"start": v(105.83, -71.97) * mm, "end": v(105.83, -80.43) * mm});
            skLineSegment(sketch, "E325.2.2.22", {"start": v(88.9, -63.5) * mm, "end": v(63.5, -63.5) * mm});
            skLineSegment(sketch, "E325.2.2.23", {"start": v(105.83, -46.57) * mm, "end": v(105.83, -55.03) * mm});
            skLineSegment(sketch, "E325.2.2.24", {"start": v(105.83, -80.43) * mm, "end": v(97.37, -80.43) * mm});
            skLineSegment(sketch, "E325.2.2.25", {"start": v(80.43, -105.83) * mm, "end": v(71.97, -105.83) * mm});
            skLineSegment(sketch, "E325.2.2.26", {"start": v(55.03, -80.43) * mm, "end": v(46.57, -80.43) * mm});
            skLineSegment(sketch, "E325.2.2.27", {"start": v(55.03, -71.97) * mm, "end": v(46.57, -71.97) * mm});
            skLineSegment(sketch, "E325.2.2.28", {"start": v(80.43, -55.03) * mm, "end": v(71.97, -55.03) * mm});
            skPoint(sketch, "E325.2.2.29", {"position": v(101.6, -101.6) * mm});
            skLineSegment(sketch, "E325.2.2.30", {"start": v(105.83, -46.57) * mm, "end": v(97.37, -46.57) * mm});
            skLineSegment(sketch, "E325.2.2.31", {"start": v(46.57, -46.57) * mm, "end": v(46.57, -55.03) * mm});
            skLineSegment(sketch, "E325.2.2.32", {"start": v(88.9, -88.9) * mm, "end": v(63.5, -88.9) * mm});
            skLineSegment(sketch, "E325.2.2.33", {"start": v(105.83, -71.97) * mm, "end": v(97.37, -71.97) * mm});
            skPoint(sketch, "E325.2.2.34", {"position": v(76.2, -101.6) * mm});
            skLineSegment(sketch, "E325.2.2.35", {"start": v(105.83, -105.83) * mm, "end": v(97.37, -105.83) * mm});
            skLineSegment(sketch, "E325.2.2.36", {"start": v(55.03, -105.83) * mm, "end": v(46.57, -105.83) * mm});
            skLineSegment(sketch, "E325.2.2.37", {"start": v(88.9, -63.5) * mm, "end": v(88.9, -88.9) * mm});
            skLineSegment(sketch, "E325.2.2.38", {"start": v(80.43, -46.57) * mm, "end": v(80.43, -55.03) * mm});
            skLineSegment(sketch, "E325.2.2.39", {"start": v(105.83, -97.37) * mm, "end": v(97.37, -97.37) * mm});
            skPoint(sketch, "E325.2.2.40", {"position": v(50.8, -50.8) * mm});
            skLineSegment(sketch, "E325.2.2.41", {"start": v(63.5, -63.5) * mm, "end": v(63.5, -88.9) * mm});
            skPoint(sketch, "E325.2.2.42", {"position": v(76.2, -50.8) * mm});
            skLineSegment(sketch, "E325.2.2.43", {"start": v(80.43, -97.37) * mm, "end": v(71.97, -97.37) * mm});
            skPoint(sketch, "E325.2.2.44", {"position": v(50.8, -76.2) * mm});
            skLineSegment(sketch, "E325.2.2.45", {"start": v(55.03, -55.03) * mm, "end": v(46.57, -55.03) * mm});
            skPoint(sketch, "E325.2.2.46", {"position": v(101.6, -101.6) * mm});
            skPoint(sketch, "E325.2.2.47", {"position": v(101.6, -50.8) * mm});
            skPoint(sketch, "E325.2.2.48", {"position": v(101.6, -76.2) * mm});
            skPoint(sketch, "E325.2.2.49", {"position": v(76.2, -50.8) * mm});
            skPoint(sketch, "E325.2.2.50", {"position": v(50.8, -101.6) * mm});
            skPoint(sketch, "E325.2.2.51", {"position": v(50.8, -50.8) * mm});
            skPoint(sketch, "E325.2.2.52", {"position": v(76.2, -101.6) * mm});
            skLineSegment(sketch, "E325.2.2.53", {"start": v(46.57, -71.97) * mm, "end": v(46.57, -80.43) * mm});
            skPoint(sketch, "E325.2.2.54", {"position": v(50.8, -76.2) * mm});
            skPoint(sketch, "E325.2.2.55", {"position": v(76.2, -50.8) * mm});
            skLineSegment(sketch, "E325.direction1", {"start": v(-105.83, 46.57) * mm, "end": v(-29.63, 46.57) * mm, "construction": true});
            skLineSegment(sketch, "E325.direction2", {"start": v(-105.83, 46.57) * mm, "end": v(-105.83, -29.63) * mm, "construction": true});
            skSolve(sketch);
        }
        {
            var Q0;
            Q0 = qSketchRegion(id + "F15", true);
            extrude(context, id + "F16", {"entities" : qUnion([Q0]), "operationType" : NewBodyOperationType.REMOVE, "oppositeDirection" : true, "depth" : 228.6 * mm, "offsetDistance" : 25.4 * mm});
        }
    });
